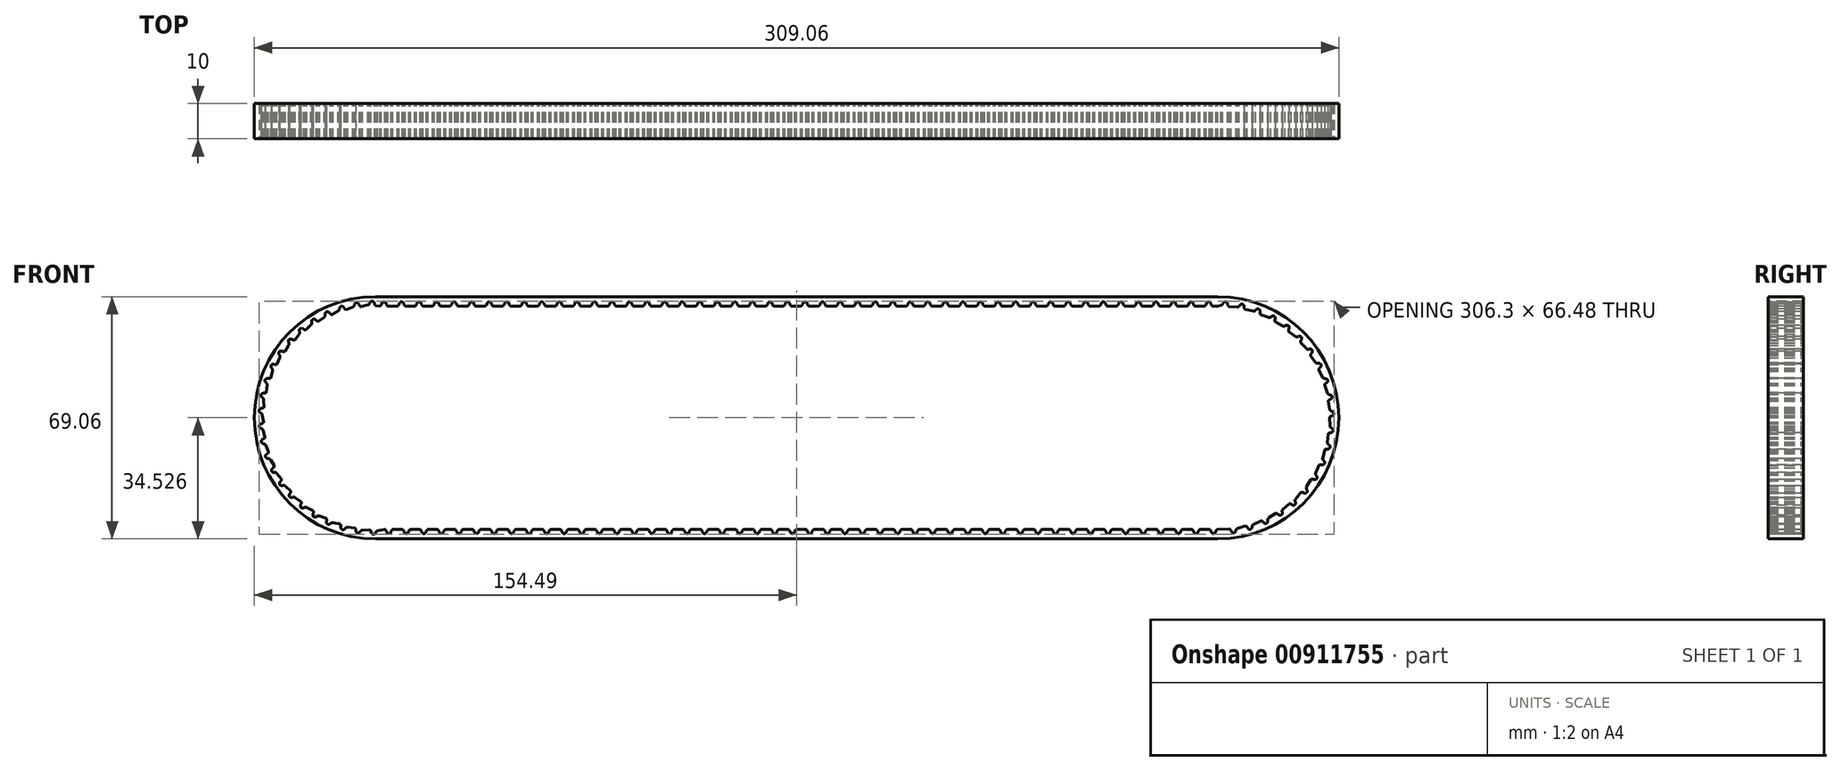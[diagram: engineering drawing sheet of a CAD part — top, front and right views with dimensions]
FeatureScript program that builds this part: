
annotation { "Feature Type Name" : "Feature", "Feature Type Description" : "" }
export const myFeature = defineFeature(function(context is Context, id is Id, definition is map)
    precondition{}
    {
        {
            var Q0;
            Q0=qCreatedBy(makeId("Front.planeOp"),FACE);
            var sketch = newSketch(context, id + "F0", { "sketchPlane" : qUnion([Q0])});
            skArc(sketch, "E0", {"start": v(-146.65, 34.53) * mm, "mid": v(-181.18, 0) * mm, "end": v(-146.65, -34.53) * mm});
            skArc(sketch, "E1", {"start": v(93.35, -34.53) * mm, "mid": v(127.88, 0) * mm, "end": v(93.35, 34.53) * mm});
            skLineSegment(sketch, "E2", {"start": v(93.35, 34.53) * mm, "end": v(-146.65, 34.53) * mm});
            skLineSegment(sketch, "E3", {"start": v(-146.65, 31.83) * mm, "end": v(-146.52, 31.83) * mm});
            skLineSegment(sketch, "E4", {"start": v(93.35, -34.53) * mm, "end": v(-146.65, -34.53) * mm});
            skLineSegment(sketch, "E5", {"start": v(93.35, -31.83) * mm, "end": v(-144, -31.83) * mm});
            skEllipticalArc(sketch, "E6.8.0.0", {});
            skArc(sketch, "E6.8.0.2", {"start": v(-103.52, 32.27) * mm, "mid": v(-103.35, 32) * mm, "end": v(-103.1, 31.83) * mm});
            skEllipticalArc(sketch, "E7.0.7.0", {});
            skArc(sketch, "E7.4.7.0", {"start": v(-105.44, 31.83) * mm, "mid": v(-105.14, 32) * mm, "end": v(-104.95, 32.27) * mm});
            skEllipticalArc(sketch, "E8.1.0.0", {});
            skArc(sketch, "E8.1.0.1", {"start": v(-98.52, 32.27) * mm, "mid": v(-98.35, 32) * mm, "end": v(-98.1, 31.83) * mm});
            skArc(sketch, "E8.1.0.2", {"start": v(-100.44, 31.83) * mm, "mid": v(-100.14, 32) * mm, "end": v(-99.95, 32.27) * mm});
            skEllipticalArc(sketch, "E8.1.0.3", {});
            skEllipticalArc(sketch, "E8.2.0.0", {});
            skArc(sketch, "E8.2.0.1", {"start": v(-93.52, 32.27) * mm, "mid": v(-93.35, 32) * mm, "end": v(-93.1, 31.83) * mm});
            skArc(sketch, "E8.2.0.2", {"start": v(-95.44, 31.83) * mm, "mid": v(-95.14, 32) * mm, "end": v(-94.95, 32.27) * mm});
            skEllipticalArc(sketch, "E8.2.0.3", {});
            skEllipticalArc(sketch, "E8.3.0.0", {});
            skArc(sketch, "E8.3.0.1", {"start": v(-88.52, 32.27) * mm, "mid": v(-88.35, 32) * mm, "end": v(-88.1, 31.83) * mm});
            skArc(sketch, "E8.3.0.2", {"start": v(-90.44, 31.83) * mm, "mid": v(-90.14, 32) * mm, "end": v(-89.95, 32.27) * mm});
            skEllipticalArc(sketch, "E8.3.0.3", {});
            skEllipticalArc(sketch, "E8.4.0.0", {});
            skArc(sketch, "E8.4.0.1", {"start": v(-83.52, 32.27) * mm, "mid": v(-83.35, 32) * mm, "end": v(-83.1, 31.83) * mm});
            skArc(sketch, "E8.4.0.2", {"start": v(-85.44, 31.83) * mm, "mid": v(-85.14, 32) * mm, "end": v(-84.95, 32.27) * mm});
            skEllipticalArc(sketch, "E8.4.0.3", {});
            skEllipticalArc(sketch, "E8.5.0.0", {});
            skArc(sketch, "E8.5.0.1", {"start": v(-78.52, 32.27) * mm, "mid": v(-78.35, 32) * mm, "end": v(-78.1, 31.83) * mm});
            skArc(sketch, "E8.5.0.2", {"start": v(-80.44, 31.83) * mm, "mid": v(-80.14, 32) * mm, "end": v(-79.95, 32.27) * mm});
            skEllipticalArc(sketch, "E8.5.0.3", {});
            skEllipticalArc(sketch, "E8.6.0.0", {});
            skArc(sketch, "E8.6.0.1", {"start": v(-73.52, 32.27) * mm, "mid": v(-73.35, 32) * mm, "end": v(-73.1, 31.83) * mm});
            skArc(sketch, "E8.6.0.2", {"start": v(-75.44, 31.83) * mm, "mid": v(-75.14, 32) * mm, "end": v(-74.95, 32.27) * mm});
            skEllipticalArc(sketch, "E8.6.0.3", {});
            skEllipticalArc(sketch, "E8.7.0.0", {});
            skArc(sketch, "E8.7.0.1", {"start": v(-68.52, 32.27) * mm, "mid": v(-68.35, 32) * mm, "end": v(-68.1, 31.83) * mm});
            skArc(sketch, "E8.7.0.2", {"start": v(-70.44, 31.83) * mm, "mid": v(-70.14, 32) * mm, "end": v(-69.95, 32.27) * mm});
            skEllipticalArc(sketch, "E8.7.0.3", {});
            skEllipticalArc(sketch, "E8.8.0.0", {});
            skArc(sketch, "E8.8.0.1", {"start": v(-63.52, 32.27) * mm, "mid": v(-63.35, 32) * mm, "end": v(-63.1, 31.83) * mm});
            skArc(sketch, "E8.8.0.2", {"start": v(-65.44, 31.83) * mm, "mid": v(-65.14, 32) * mm, "end": v(-64.95, 32.27) * mm});
            skEllipticalArc(sketch, "E8.8.0.3", {});
            skEllipticalArc(sketch, "E8.9.0.0", {});
            skArc(sketch, "E8.9.0.1", {"start": v(-58.52, 32.27) * mm, "mid": v(-58.35, 32) * mm, "end": v(-58.1, 31.83) * mm});
            skArc(sketch, "E8.9.0.2", {"start": v(-60.44, 31.83) * mm, "mid": v(-60.14, 32) * mm, "end": v(-59.95, 32.27) * mm});
            skEllipticalArc(sketch, "E8.9.0.3", {});
            skEllipticalArc(sketch, "E8.10.0.0", {});
            skArc(sketch, "E8.10.0.1", {"start": v(-53.52, 32.27) * mm, "mid": v(-53.35, 32) * mm, "end": v(-53.1, 31.83) * mm});
            skArc(sketch, "E8.10.0.2", {"start": v(-55.44, 31.83) * mm, "mid": v(-55.14, 32) * mm, "end": v(-54.95, 32.27) * mm});
            skEllipticalArc(sketch, "E8.10.0.3", {});
            skEllipticalArc(sketch, "E8.11.0.0", {});
            skArc(sketch, "E8.11.0.1", {"start": v(-48.52, 32.27) * mm, "mid": v(-48.35, 32) * mm, "end": v(-48.1, 31.83) * mm});
            skArc(sketch, "E8.11.0.2", {"start": v(-50.44, 31.83) * mm, "mid": v(-50.14, 32) * mm, "end": v(-49.95, 32.27) * mm});
            skEllipticalArc(sketch, "E8.11.0.3", {});
            skEllipticalArc(sketch, "E8.12.0.0", {});
            skArc(sketch, "E8.12.0.1", {"start": v(-43.52, 32.27) * mm, "mid": v(-43.35, 32) * mm, "end": v(-43.1, 31.83) * mm});
            skArc(sketch, "E8.12.0.2", {"start": v(-45.44, 31.83) * mm, "mid": v(-45.14, 32) * mm, "end": v(-44.95, 32.27) * mm});
            skEllipticalArc(sketch, "E8.12.0.3", {});
            skEllipticalArc(sketch, "E8.13.0.0", {});
            skArc(sketch, "E8.13.0.1", {"start": v(-38.52, 32.27) * mm, "mid": v(-38.35, 32) * mm, "end": v(-38.1, 31.83) * mm});
            skArc(sketch, "E8.13.0.2", {"start": v(-40.44, 31.83) * mm, "mid": v(-40.14, 32) * mm, "end": v(-39.95, 32.27) * mm});
            skEllipticalArc(sketch, "E8.13.0.3", {});
            skEllipticalArc(sketch, "E8.14.0.0", {});
            skArc(sketch, "E8.14.0.1", {"start": v(-33.52, 32.27) * mm, "mid": v(-33.35, 32) * mm, "end": v(-33.1, 31.83) * mm});
            skArc(sketch, "E8.14.0.2", {"start": v(-35.44, 31.83) * mm, "mid": v(-35.14, 32) * mm, "end": v(-34.95, 32.27) * mm});
            skEllipticalArc(sketch, "E8.14.0.3", {});
            skEllipticalArc(sketch, "E8.15.0.0", {});
            skArc(sketch, "E8.15.0.1", {"start": v(-28.52, 32.27) * mm, "mid": v(-28.35, 32) * mm, "end": v(-28.1, 31.83) * mm});
            skArc(sketch, "E8.15.0.2", {"start": v(-30.44, 31.83) * mm, "mid": v(-30.14, 32) * mm, "end": v(-29.95, 32.27) * mm});
            skEllipticalArc(sketch, "E8.15.0.3", {});
            skEllipticalArc(sketch, "E8.16.0.0", {});
            skArc(sketch, "E8.16.0.1", {"start": v(-23.52, 32.27) * mm, "mid": v(-23.35, 32) * mm, "end": v(-23.1, 31.83) * mm});
            skArc(sketch, "E8.16.0.2", {"start": v(-25.44, 31.83) * mm, "mid": v(-25.14, 32) * mm, "end": v(-24.95, 32.27) * mm});
            skEllipticalArc(sketch, "E8.16.0.3", {});
            skEllipticalArc(sketch, "E8.17.0.0", {});
            skArc(sketch, "E8.17.0.1", {"start": v(-18.52, 32.27) * mm, "mid": v(-18.35, 32) * mm, "end": v(-18.1, 31.83) * mm});
            skArc(sketch, "E8.17.0.2", {"start": v(-20.44, 31.83) * mm, "mid": v(-20.14, 32) * mm, "end": v(-19.95, 32.27) * mm});
            skEllipticalArc(sketch, "E8.17.0.3", {});
            skEllipticalArc(sketch, "E8.18.0.0", {});
            skArc(sketch, "E8.18.0.1", {"start": v(-13.52, 32.27) * mm, "mid": v(-13.35, 32) * mm, "end": v(-13.1, 31.83) * mm});
            skArc(sketch, "E8.18.0.2", {"start": v(-15.44, 31.83) * mm, "mid": v(-15.14, 32) * mm, "end": v(-14.95, 32.27) * mm});
            skEllipticalArc(sketch, "E8.18.0.3", {});
            skEllipticalArc(sketch, "E8.19.0.0", {});
            skArc(sketch, "E8.19.0.1", {"start": v(-8.52, 32.27) * mm, "mid": v(-8.35, 32) * mm, "end": v(-8.1, 31.83) * mm});
            skArc(sketch, "E8.19.0.2", {"start": v(-10.44, 31.83) * mm, "mid": v(-10.14, 32) * mm, "end": v(-9.95, 32.27) * mm});
            skEllipticalArc(sketch, "E8.19.0.3", {});
            skEllipticalArc(sketch, "E8.20.0.0", {});
            skArc(sketch, "E8.20.0.1", {"start": v(-3.52, 32.27) * mm, "mid": v(-3.35, 32) * mm, "end": v(-3.1, 31.83) * mm});
            skArc(sketch, "E8.20.0.2", {"start": v(-5.44, 31.83) * mm, "mid": v(-5.14, 32) * mm, "end": v(-4.95, 32.27) * mm});
            skEllipticalArc(sketch, "E8.20.0.3", {});
            skEllipticalArc(sketch, "E8.21.0.0", {});
            skArc(sketch, "E8.21.0.1", {"start": v(1.48, 32.27) * mm, "mid": v(1.65, 32) * mm, "end": v(1.9, 31.83) * mm});
            skArc(sketch, "E8.21.0.2", {"start": v(-0.44, 31.83) * mm, "mid": v(-0.14, 32) * mm, "end": v(0.05, 32.27) * mm});
            skEllipticalArc(sketch, "E8.21.0.3", {});
            skEllipticalArc(sketch, "E8.22.0.0", {});
            skArc(sketch, "E8.22.0.1", {"start": v(6.48, 32.27) * mm, "mid": v(6.65, 32) * mm, "end": v(6.9, 31.83) * mm});
            skArc(sketch, "E8.22.0.2", {"start": v(4.56, 31.83) * mm, "mid": v(4.86, 32) * mm, "end": v(5.05, 32.27) * mm});
            skEllipticalArc(sketch, "E8.22.0.3", {});
            skEllipticalArc(sketch, "E8.23.0.0", {});
            skArc(sketch, "E8.23.0.1", {"start": v(11.48, 32.27) * mm, "mid": v(11.65, 32) * mm, "end": v(11.9, 31.83) * mm});
            skArc(sketch, "E8.23.0.2", {"start": v(9.56, 31.83) * mm, "mid": v(9.86, 32) * mm, "end": v(10.05, 32.27) * mm});
            skEllipticalArc(sketch, "E8.23.0.3", {});
            skEllipticalArc(sketch, "E8.24.0.0", {});
            skArc(sketch, "E8.24.0.1", {"start": v(16.48, 32.27) * mm, "mid": v(16.65, 32) * mm, "end": v(16.9, 31.83) * mm});
            skArc(sketch, "E8.24.0.2", {"start": v(14.56, 31.83) * mm, "mid": v(14.86, 32) * mm, "end": v(15.05, 32.27) * mm});
            skEllipticalArc(sketch, "E8.24.0.3", {});
            skEllipticalArc(sketch, "E8.25.0.0", {});
            skArc(sketch, "E8.25.0.1", {"start": v(21.48, 32.27) * mm, "mid": v(21.65, 32) * mm, "end": v(21.9, 31.83) * mm});
            skArc(sketch, "E8.25.0.2", {"start": v(19.56, 31.83) * mm, "mid": v(19.86, 32) * mm, "end": v(20.05, 32.27) * mm});
            skEllipticalArc(sketch, "E8.25.0.3", {});
            skEllipticalArc(sketch, "E8.26.0.0", {});
            skArc(sketch, "E8.26.0.1", {"start": v(26.48, 32.27) * mm, "mid": v(26.65, 32) * mm, "end": v(26.9, 31.83) * mm});
            skArc(sketch, "E8.26.0.2", {"start": v(24.56, 31.83) * mm, "mid": v(24.86, 32) * mm, "end": v(25.05, 32.27) * mm});
            skEllipticalArc(sketch, "E8.26.0.3", {});
            skEllipticalArc(sketch, "E8.27.0.0", {});
            skArc(sketch, "E8.27.0.1", {"start": v(31.48, 32.27) * mm, "mid": v(31.65, 32) * mm, "end": v(31.9, 31.83) * mm});
            skArc(sketch, "E8.27.0.2", {"start": v(29.56, 31.83) * mm, "mid": v(29.86, 32) * mm, "end": v(30.05, 32.27) * mm});
            skEllipticalArc(sketch, "E8.27.0.3", {});
            skEllipticalArc(sketch, "E8.28.0.0", {});
            skArc(sketch, "E8.28.0.1", {"start": v(36.48, 32.27) * mm, "mid": v(36.65, 32) * mm, "end": v(36.9, 31.83) * mm});
            skArc(sketch, "E8.28.0.2", {"start": v(34.56, 31.83) * mm, "mid": v(34.86, 32) * mm, "end": v(35.05, 32.27) * mm});
            skEllipticalArc(sketch, "E8.28.0.3", {});
            skEllipticalArc(sketch, "E8.29.0.0", {});
            skArc(sketch, "E8.29.0.1", {"start": v(41.48, 32.27) * mm, "mid": v(41.65, 32) * mm, "end": v(41.9, 31.83) * mm});
            skArc(sketch, "E8.29.0.2", {"start": v(39.56, 31.83) * mm, "mid": v(39.86, 32) * mm, "end": v(40.05, 32.27) * mm});
            skEllipticalArc(sketch, "E8.29.0.3", {});
            skEllipticalArc(sketch, "E8.30.0.0", {});
            skArc(sketch, "E8.30.0.1", {"start": v(46.48, 32.27) * mm, "mid": v(46.65, 32) * mm, "end": v(46.9, 31.83) * mm});
            skArc(sketch, "E8.30.0.2", {"start": v(44.56, 31.83) * mm, "mid": v(44.86, 32) * mm, "end": v(45.05, 32.27) * mm});
            skEllipticalArc(sketch, "E8.30.0.3", {});
            skEllipticalArc(sketch, "E8.31.0.0", {});
            skArc(sketch, "E8.31.0.1", {"start": v(51.48, 32.27) * mm, "mid": v(51.65, 32) * mm, "end": v(51.9, 31.83) * mm});
            skArc(sketch, "E8.31.0.2", {"start": v(49.56, 31.83) * mm, "mid": v(49.86, 32) * mm, "end": v(50.05, 32.27) * mm});
            skEllipticalArc(sketch, "E8.31.0.3", {});
            skEllipticalArc(sketch, "E8.32.0.0", {});
            skArc(sketch, "E8.32.0.1", {"start": v(56.48, 32.27) * mm, "mid": v(56.65, 32) * mm, "end": v(56.9, 31.83) * mm});
            skArc(sketch, "E8.32.0.2", {"start": v(54.56, 31.83) * mm, "mid": v(54.86, 32) * mm, "end": v(55.05, 32.27) * mm});
            skEllipticalArc(sketch, "E8.32.0.3", {});
            skEllipticalArc(sketch, "E8.33.0.0", {});
            skArc(sketch, "E8.33.0.1", {"start": v(61.48, 32.27) * mm, "mid": v(61.65, 32) * mm, "end": v(61.9, 31.83) * mm});
            skArc(sketch, "E8.33.0.2", {"start": v(59.56, 31.83) * mm, "mid": v(59.86, 32) * mm, "end": v(60.05, 32.27) * mm});
            skEllipticalArc(sketch, "E8.33.0.3", {});
            skEllipticalArc(sketch, "E8.34.0.0", {});
            skArc(sketch, "E8.34.0.1", {"start": v(66.48, 32.27) * mm, "mid": v(66.65, 32) * mm, "end": v(66.9, 31.83) * mm});
            skArc(sketch, "E8.34.0.2", {"start": v(64.56, 31.83) * mm, "mid": v(64.86, 32) * mm, "end": v(65.05, 32.27) * mm});
            skEllipticalArc(sketch, "E8.34.0.3", {});
            skEllipticalArc(sketch, "E8.35.0.0", {});
            skArc(sketch, "E8.35.0.1", {"start": v(71.48, 32.27) * mm, "mid": v(71.65, 32) * mm, "end": v(71.9, 31.83) * mm});
            skArc(sketch, "E8.35.0.2", {"start": v(69.56, 31.83) * mm, "mid": v(69.86, 32) * mm, "end": v(70.05, 32.27) * mm});
            skEllipticalArc(sketch, "E8.35.0.3", {});
            skEllipticalArc(sketch, "E8.36.0.0", {});
            skArc(sketch, "E8.36.0.1", {"start": v(76.48, 32.27) * mm, "mid": v(76.65, 32) * mm, "end": v(76.9, 31.83) * mm});
            skArc(sketch, "E8.36.0.2", {"start": v(74.56, 31.83) * mm, "mid": v(74.86, 32) * mm, "end": v(75.05, 32.27) * mm});
            skEllipticalArc(sketch, "E8.36.0.3", {});
            skEllipticalArc(sketch, "E8.37.0.0", {});
            skArc(sketch, "E8.37.0.1", {"start": v(81.48, 32.27) * mm, "mid": v(81.65, 32) * mm, "end": v(81.9, 31.83) * mm});
            skArc(sketch, "E8.37.0.2", {"start": v(79.56, 31.83) * mm, "mid": v(79.86, 32) * mm, "end": v(80.05, 32.27) * mm});
            skEllipticalArc(sketch, "E8.37.0.3", {});
            skEllipticalArc(sketch, "E8.38.0.0", {});
            skArc(sketch, "E8.38.0.1", {"start": v(86.48, 32.27) * mm, "mid": v(86.65, 32) * mm, "end": v(86.9, 31.83) * mm});
            skArc(sketch, "E8.38.0.2", {"start": v(84.56, 31.83) * mm, "mid": v(84.86, 32) * mm, "end": v(85.05, 32.27) * mm});
            skEllipticalArc(sketch, "E8.38.0.3", {});
            skEllipticalArc(sketch, "E8.39.0.0", {});
            skArc(sketch, "E8.39.0.1", {"start": v(91.48, 32.27) * mm, "mid": v(91.65, 32) * mm, "end": v(91.9, 31.83) * mm});
            skArc(sketch, "E8.39.0.2", {"start": v(89.56, 31.83) * mm, "mid": v(89.86, 32) * mm, "end": v(90.05, 32.27) * mm});
            skEllipticalArc(sketch, "E8.39.0.3", {});
            skLineSegment(sketch, "E8.direction1", {"start": v(-105.44, 31.83) * mm, "end": v(-100.44, 31.83) * mm, "construction": true});
            skArc(sketch, "E9.1.0.0", {"start": v(-108.52, 32.27) * mm, "mid": v(-108.35, 32) * mm, "end": v(-108.1, 31.83) * mm});
            skEllipticalArc(sketch, "E9.1.0.1", {});
            skEllipticalArc(sketch, "E9.1.0.2", {});
            skArc(sketch, "E9.1.0.3", {"start": v(-110.44, 31.83) * mm, "mid": v(-110.14, 32) * mm, "end": v(-109.95, 32.27) * mm});
            skArc(sketch, "E9.2.0.0", {"start": v(-113.52, 32.27) * mm, "mid": v(-113.35, 32) * mm, "end": v(-113.1, 31.83) * mm});
            skEllipticalArc(sketch, "E9.2.0.1", {});
            skEllipticalArc(sketch, "E9.2.0.2", {});
            skArc(sketch, "E9.2.0.3", {"start": v(-115.44, 31.83) * mm, "mid": v(-115.14, 32) * mm, "end": v(-114.95, 32.27) * mm});
            skArc(sketch, "E9.3.0.0", {"start": v(-118.52, 32.27) * mm, "mid": v(-118.35, 32) * mm, "end": v(-118.1, 31.83) * mm});
            skEllipticalArc(sketch, "E9.3.0.1", {});
            skEllipticalArc(sketch, "E9.3.0.2", {});
            skArc(sketch, "E9.3.0.3", {"start": v(-120.44, 31.83) * mm, "mid": v(-120.14, 32) * mm, "end": v(-119.95, 32.27) * mm});
            skArc(sketch, "E9.4.0.0", {"start": v(-123.52, 32.27) * mm, "mid": v(-123.35, 32) * mm, "end": v(-123.1, 31.83) * mm});
            skEllipticalArc(sketch, "E9.4.0.1", {});
            skEllipticalArc(sketch, "E9.4.0.2", {});
            skArc(sketch, "E9.4.0.3", {"start": v(-125.44, 31.83) * mm, "mid": v(-125.14, 32) * mm, "end": v(-124.95, 32.27) * mm});
            skArc(sketch, "E9.5.0.0", {"start": v(-128.52, 32.27) * mm, "mid": v(-128.35, 32) * mm, "end": v(-128.1, 31.83) * mm});
            skEllipticalArc(sketch, "E9.5.0.1", {});
            skEllipticalArc(sketch, "E9.5.0.2", {});
            skArc(sketch, "E9.5.0.3", {"start": v(-130.44, 31.83) * mm, "mid": v(-130.14, 32) * mm, "end": v(-129.95, 32.27) * mm});
            skArc(sketch, "E9.6.0.0", {"start": v(-133.52, 32.27) * mm, "mid": v(-133.35, 32) * mm, "end": v(-133.1, 31.83) * mm});
            skEllipticalArc(sketch, "E9.6.0.1", {});
            skEllipticalArc(sketch, "E9.6.0.2", {});
            skArc(sketch, "E9.6.0.3", {"start": v(-135.44, 31.83) * mm, "mid": v(-135.14, 32) * mm, "end": v(-134.95, 32.27) * mm});
            skArc(sketch, "E9.7.0.0", {"start": v(-138.52, 32.27) * mm, "mid": v(-138.35, 32) * mm, "end": v(-138.1, 31.83) * mm});
            skEllipticalArc(sketch, "E9.7.0.1", {});
            skEllipticalArc(sketch, "E9.7.0.2", {});
            skArc(sketch, "E9.7.0.3", {"start": v(-140.44, 31.83) * mm, "mid": v(-140.14, 32) * mm, "end": v(-139.95, 32.27) * mm});
            skArc(sketch, "E9.8.0.0", {"start": v(-143.52, 32.27) * mm, "mid": v(-143.35, 32) * mm, "end": v(-143.1, 31.83) * mm});
            skEllipticalArc(sketch, "E9.8.0.1", {});
            skEllipticalArc(sketch, "E9.8.0.2", {});
            skArc(sketch, "E9.8.0.3", {"start": v(-145.44, 31.83) * mm, "mid": v(-145.14, 32) * mm, "end": v(-144.95, 32.27) * mm});
            skLineSegment(sketch, "E9.direction1", {"start": v(-103.1, 31.83) * mm, "end": v(-108.1, 31.83) * mm, "construction": true});
            skEllipticalArc(sketch, "E10.8.0.0", {});
            skArc(sketch, "E10.8.0.2", {"start": v(51.43, -32.27) * mm, "mid": v(51.26, -32) * mm, "end": v(51, -31.83) * mm});
            skEllipticalArc(sketch, "E11.0.7.0", {});
            skArc(sketch, "E11.4.7.0", {"start": v(53.35, -31.83) * mm, "mid": v(53.05, -32) * mm, "end": v(52.85, -32.27) * mm});
            skEllipticalArc(sketch, "E12.1.0.0", {});
            skArc(sketch, "E12.1.0.1", {"start": v(46.43, -32.27) * mm, "mid": v(46.26, -32) * mm, "end": v(46, -31.83) * mm});
            skArc(sketch, "E12.1.0.2", {"start": v(48.35, -31.83) * mm, "mid": v(48.05, -32) * mm, "end": v(47.85, -32.27) * mm});
            skEllipticalArc(sketch, "E12.1.0.3", {});
            skEllipticalArc(sketch, "E12.2.0.0", {});
            skArc(sketch, "E12.2.0.1", {"start": v(41.43, -32.27) * mm, "mid": v(41.26, -32) * mm, "end": v(41, -31.83) * mm});
            skArc(sketch, "E12.2.0.2", {"start": v(43.35, -31.83) * mm, "mid": v(43.05, -32) * mm, "end": v(42.85, -32.27) * mm});
            skEllipticalArc(sketch, "E12.2.0.3", {});
            skEllipticalArc(sketch, "E12.3.0.0", {});
            skArc(sketch, "E12.3.0.1", {"start": v(36.43, -32.27) * mm, "mid": v(36.26, -32) * mm, "end": v(36, -31.83) * mm});
            skArc(sketch, "E12.3.0.2", {"start": v(38.35, -31.83) * mm, "mid": v(38.05, -32) * mm, "end": v(37.85, -32.27) * mm});
            skEllipticalArc(sketch, "E12.3.0.3", {});
            skEllipticalArc(sketch, "E12.4.0.0", {});
            skArc(sketch, "E12.4.0.1", {"start": v(31.43, -32.27) * mm, "mid": v(31.26, -32) * mm, "end": v(31, -31.83) * mm});
            skArc(sketch, "E12.4.0.2", {"start": v(33.35, -31.83) * mm, "mid": v(33.05, -32) * mm, "end": v(32.85, -32.27) * mm});
            skEllipticalArc(sketch, "E12.4.0.3", {});
            skEllipticalArc(sketch, "E12.5.0.0", {});
            skArc(sketch, "E12.5.0.1", {"start": v(26.43, -32.27) * mm, "mid": v(26.26, -32) * mm, "end": v(26, -31.83) * mm});
            skArc(sketch, "E12.5.0.2", {"start": v(28.35, -31.83) * mm, "mid": v(28.05, -32) * mm, "end": v(27.85, -32.27) * mm});
            skEllipticalArc(sketch, "E12.5.0.3", {});
            skEllipticalArc(sketch, "E12.6.0.0", {});
            skArc(sketch, "E12.6.0.1", {"start": v(21.43, -32.27) * mm, "mid": v(21.26, -32) * mm, "end": v(21, -31.83) * mm});
            skArc(sketch, "E12.6.0.2", {"start": v(23.35, -31.83) * mm, "mid": v(23.05, -32) * mm, "end": v(22.85, -32.27) * mm});
            skEllipticalArc(sketch, "E12.6.0.3", {});
            skEllipticalArc(sketch, "E12.7.0.0", {});
            skArc(sketch, "E12.7.0.1", {"start": v(16.43, -32.27) * mm, "mid": v(16.26, -32) * mm, "end": v(16, -31.83) * mm});
            skArc(sketch, "E12.7.0.2", {"start": v(18.35, -31.83) * mm, "mid": v(18.05, -32) * mm, "end": v(17.85, -32.27) * mm});
            skEllipticalArc(sketch, "E12.7.0.3", {});
            skEllipticalArc(sketch, "E12.8.0.0", {});
            skArc(sketch, "E12.8.0.1", {"start": v(11.43, -32.27) * mm, "mid": v(11.26, -32) * mm, "end": v(11, -31.83) * mm});
            skArc(sketch, "E12.8.0.2", {"start": v(13.35, -31.83) * mm, "mid": v(13.05, -32) * mm, "end": v(12.85, -32.27) * mm});
            skEllipticalArc(sketch, "E12.8.0.3", {});
            skEllipticalArc(sketch, "E12.9.0.0", {});
            skArc(sketch, "E12.9.0.1", {"start": v(6.43, -32.27) * mm, "mid": v(6.26, -32) * mm, "end": v(6, -31.83) * mm});
            skArc(sketch, "E12.9.0.2", {"start": v(8.35, -31.83) * mm, "mid": v(8.05, -32) * mm, "end": v(7.85, -32.27) * mm});
            skEllipticalArc(sketch, "E12.9.0.3", {});
            skEllipticalArc(sketch, "E12.10.0.0", {});
            skArc(sketch, "E12.10.0.1", {"start": v(1.43, -32.27) * mm, "mid": v(1.26, -32) * mm, "end": v(1, -31.83) * mm});
            skArc(sketch, "E12.10.0.2", {"start": v(3.35, -31.83) * mm, "mid": v(3.05, -32) * mm, "end": v(2.85, -32.27) * mm});
            skEllipticalArc(sketch, "E12.10.0.3", {});
            skEllipticalArc(sketch, "E12.11.0.0", {});
            skArc(sketch, "E12.11.0.1", {"start": v(-3.57, -32.27) * mm, "mid": v(-3.74, -32) * mm, "end": v(-4, -31.83) * mm});
            skArc(sketch, "E12.11.0.2", {"start": v(-1.65, -31.83) * mm, "mid": v(-1.95, -32) * mm, "end": v(-2.15, -32.27) * mm});
            skEllipticalArc(sketch, "E12.11.0.3", {});
            skEllipticalArc(sketch, "E12.12.0.0", {});
            skArc(sketch, "E12.12.0.1", {"start": v(-8.57, -32.27) * mm, "mid": v(-8.74, -32) * mm, "end": v(-9, -31.83) * mm});
            skArc(sketch, "E12.12.0.2", {"start": v(-6.65, -31.83) * mm, "mid": v(-6.95, -32) * mm, "end": v(-7.15, -32.27) * mm});
            skEllipticalArc(sketch, "E12.12.0.3", {});
            skEllipticalArc(sketch, "E12.13.0.0", {});
            skArc(sketch, "E12.13.0.1", {"start": v(-13.57, -32.27) * mm, "mid": v(-13.74, -32) * mm, "end": v(-14, -31.83) * mm});
            skArc(sketch, "E12.13.0.2", {"start": v(-11.65, -31.83) * mm, "mid": v(-11.95, -32) * mm, "end": v(-12.15, -32.27) * mm});
            skEllipticalArc(sketch, "E12.13.0.3", {});
            skEllipticalArc(sketch, "E12.14.0.0", {});
            skArc(sketch, "E12.14.0.1", {"start": v(-18.57, -32.27) * mm, "mid": v(-18.74, -32) * mm, "end": v(-19, -31.83) * mm});
            skArc(sketch, "E12.14.0.2", {"start": v(-16.65, -31.83) * mm, "mid": v(-16.95, -32) * mm, "end": v(-17.15, -32.27) * mm});
            skEllipticalArc(sketch, "E12.14.0.3", {});
            skEllipticalArc(sketch, "E12.15.0.0", {});
            skArc(sketch, "E12.15.0.1", {"start": v(-23.57, -32.27) * mm, "mid": v(-23.74, -32) * mm, "end": v(-24, -31.83) * mm});
            skArc(sketch, "E12.15.0.2", {"start": v(-21.65, -31.83) * mm, "mid": v(-21.95, -32) * mm, "end": v(-22.15, -32.27) * mm});
            skEllipticalArc(sketch, "E12.15.0.3", {});
            skEllipticalArc(sketch, "E12.16.0.0", {});
            skArc(sketch, "E12.16.0.1", {"start": v(-28.57, -32.27) * mm, "mid": v(-28.74, -32) * mm, "end": v(-29, -31.83) * mm});
            skArc(sketch, "E12.16.0.2", {"start": v(-26.65, -31.83) * mm, "mid": v(-26.95, -32) * mm, "end": v(-27.15, -32.27) * mm});
            skEllipticalArc(sketch, "E12.16.0.3", {});
            skEllipticalArc(sketch, "E12.17.0.0", {});
            skArc(sketch, "E12.17.0.1", {"start": v(-33.57, -32.27) * mm, "mid": v(-33.74, -32) * mm, "end": v(-34, -31.83) * mm});
            skArc(sketch, "E12.17.0.2", {"start": v(-31.65, -31.83) * mm, "mid": v(-31.95, -32) * mm, "end": v(-32.15, -32.27) * mm});
            skEllipticalArc(sketch, "E12.17.0.3", {});
            skEllipticalArc(sketch, "E12.18.0.0", {});
            skArc(sketch, "E12.18.0.1", {"start": v(-38.57, -32.27) * mm, "mid": v(-38.74, -32) * mm, "end": v(-39, -31.83) * mm});
            skArc(sketch, "E12.18.0.2", {"start": v(-36.65, -31.83) * mm, "mid": v(-36.95, -32) * mm, "end": v(-37.15, -32.27) * mm});
            skEllipticalArc(sketch, "E12.18.0.3", {});
            skEllipticalArc(sketch, "E12.19.0.0", {});
            skArc(sketch, "E12.19.0.1", {"start": v(-43.57, -32.27) * mm, "mid": v(-43.74, -32) * mm, "end": v(-44, -31.83) * mm});
            skArc(sketch, "E12.19.0.2", {"start": v(-41.65, -31.83) * mm, "mid": v(-41.95, -32) * mm, "end": v(-42.15, -32.27) * mm});
            skEllipticalArc(sketch, "E12.19.0.3", {});
            skEllipticalArc(sketch, "E12.20.0.0", {});
            skArc(sketch, "E12.20.0.1", {"start": v(-48.57, -32.27) * mm, "mid": v(-48.74, -32) * mm, "end": v(-49, -31.83) * mm});
            skArc(sketch, "E12.20.0.2", {"start": v(-46.65, -31.83) * mm, "mid": v(-46.95, -32) * mm, "end": v(-47.15, -32.27) * mm});
            skEllipticalArc(sketch, "E12.20.0.3", {});
            skEllipticalArc(sketch, "E12.21.0.0", {});
            skArc(sketch, "E12.21.0.1", {"start": v(-53.57, -32.27) * mm, "mid": v(-53.74, -32) * mm, "end": v(-54, -31.83) * mm});
            skArc(sketch, "E12.21.0.2", {"start": v(-51.65, -31.83) * mm, "mid": v(-51.95, -32) * mm, "end": v(-52.15, -32.27) * mm});
            skEllipticalArc(sketch, "E12.21.0.3", {});
            skEllipticalArc(sketch, "E12.22.0.0", {});
            skArc(sketch, "E12.22.0.1", {"start": v(-58.57, -32.27) * mm, "mid": v(-58.74, -32) * mm, "end": v(-59, -31.83) * mm});
            skArc(sketch, "E12.22.0.2", {"start": v(-56.65, -31.83) * mm, "mid": v(-56.95, -32) * mm, "end": v(-57.15, -32.27) * mm});
            skEllipticalArc(sketch, "E12.22.0.3", {});
            skEllipticalArc(sketch, "E12.23.0.0", {});
            skArc(sketch, "E12.23.0.1", {"start": v(-63.57, -32.27) * mm, "mid": v(-63.74, -32) * mm, "end": v(-64, -31.83) * mm});
            skArc(sketch, "E12.23.0.2", {"start": v(-61.65, -31.83) * mm, "mid": v(-61.95, -32) * mm, "end": v(-62.15, -32.27) * mm});
            skEllipticalArc(sketch, "E12.23.0.3", {});
            skEllipticalArc(sketch, "E12.24.0.0", {});
            skArc(sketch, "E12.24.0.1", {"start": v(-68.57, -32.27) * mm, "mid": v(-68.74, -32) * mm, "end": v(-69, -31.83) * mm});
            skArc(sketch, "E12.24.0.2", {"start": v(-66.65, -31.83) * mm, "mid": v(-66.95, -32) * mm, "end": v(-67.15, -32.27) * mm});
            skEllipticalArc(sketch, "E12.24.0.3", {});
            skEllipticalArc(sketch, "E12.25.0.0", {});
            skArc(sketch, "E12.25.0.1", {"start": v(-73.57, -32.27) * mm, "mid": v(-73.74, -32) * mm, "end": v(-74, -31.83) * mm});
            skArc(sketch, "E12.25.0.2", {"start": v(-71.65, -31.83) * mm, "mid": v(-71.95, -32) * mm, "end": v(-72.15, -32.27) * mm});
            skEllipticalArc(sketch, "E12.25.0.3", {});
            skEllipticalArc(sketch, "E12.26.0.0", {});
            skArc(sketch, "E12.26.0.1", {"start": v(-78.57, -32.27) * mm, "mid": v(-78.74, -32) * mm, "end": v(-79, -31.83) * mm});
            skArc(sketch, "E12.26.0.2", {"start": v(-76.65, -31.83) * mm, "mid": v(-76.95, -32) * mm, "end": v(-77.15, -32.27) * mm});
            skEllipticalArc(sketch, "E12.26.0.3", {});
            skEllipticalArc(sketch, "E12.27.0.0", {});
            skArc(sketch, "E12.27.0.1", {"start": v(-83.57, -32.27) * mm, "mid": v(-83.74, -32) * mm, "end": v(-84, -31.83) * mm});
            skArc(sketch, "E12.27.0.2", {"start": v(-81.65, -31.83) * mm, "mid": v(-81.95, -32) * mm, "end": v(-82.15, -32.27) * mm});
            skEllipticalArc(sketch, "E12.27.0.3", {});
            skEllipticalArc(sketch, "E12.28.0.0", {});
            skArc(sketch, "E12.28.0.1", {"start": v(-88.57, -32.27) * mm, "mid": v(-88.74, -32) * mm, "end": v(-89, -31.83) * mm});
            skArc(sketch, "E12.28.0.2", {"start": v(-86.65, -31.83) * mm, "mid": v(-86.95, -32) * mm, "end": v(-87.15, -32.27) * mm});
            skEllipticalArc(sketch, "E12.28.0.3", {});
            skEllipticalArc(sketch, "E12.29.0.0", {});
            skArc(sketch, "E12.29.0.1", {"start": v(-93.57, -32.27) * mm, "mid": v(-93.74, -32) * mm, "end": v(-94, -31.83) * mm});
            skArc(sketch, "E12.29.0.2", {"start": v(-91.65, -31.83) * mm, "mid": v(-91.95, -32) * mm, "end": v(-92.15, -32.27) * mm});
            skEllipticalArc(sketch, "E12.29.0.3", {});
            skEllipticalArc(sketch, "E12.30.0.0", {});
            skArc(sketch, "E12.30.0.1", {"start": v(-98.57, -32.27) * mm, "mid": v(-98.74, -32) * mm, "end": v(-99, -31.83) * mm});
            skArc(sketch, "E12.30.0.2", {"start": v(-96.65, -31.83) * mm, "mid": v(-96.95, -32) * mm, "end": v(-97.15, -32.27) * mm});
            skEllipticalArc(sketch, "E12.30.0.3", {});
            skEllipticalArc(sketch, "E12.31.0.0", {});
            skArc(sketch, "E12.31.0.1", {"start": v(-103.57, -32.27) * mm, "mid": v(-103.74, -32) * mm, "end": v(-104, -31.83) * mm});
            skArc(sketch, "E12.31.0.2", {"start": v(-101.65, -31.83) * mm, "mid": v(-101.95, -32) * mm, "end": v(-102.15, -32.27) * mm});
            skEllipticalArc(sketch, "E12.31.0.3", {});
            skEllipticalArc(sketch, "E12.32.0.0", {});
            skArc(sketch, "E12.32.0.1", {"start": v(-108.57, -32.27) * mm, "mid": v(-108.74, -32) * mm, "end": v(-109, -31.83) * mm});
            skArc(sketch, "E12.32.0.2", {"start": v(-106.65, -31.83) * mm, "mid": v(-106.95, -32) * mm, "end": v(-107.15, -32.27) * mm});
            skEllipticalArc(sketch, "E12.32.0.3", {});
            skEllipticalArc(sketch, "E12.33.0.0", {});
            skArc(sketch, "E12.33.0.1", {"start": v(-113.57, -32.27) * mm, "mid": v(-113.74, -32) * mm, "end": v(-114, -31.83) * mm});
            skArc(sketch, "E12.33.0.2", {"start": v(-111.65, -31.83) * mm, "mid": v(-111.95, -32) * mm, "end": v(-112.15, -32.27) * mm});
            skEllipticalArc(sketch, "E12.33.0.3", {});
            skEllipticalArc(sketch, "E12.34.0.0", {});
            skArc(sketch, "E12.34.0.1", {"start": v(-118.57, -32.27) * mm, "mid": v(-118.74, -32) * mm, "end": v(-119, -31.83) * mm});
            skArc(sketch, "E12.34.0.2", {"start": v(-116.65, -31.83) * mm, "mid": v(-116.95, -32) * mm, "end": v(-117.15, -32.27) * mm});
            skEllipticalArc(sketch, "E12.34.0.3", {});
            skEllipticalArc(sketch, "E12.35.0.0", {});
            skArc(sketch, "E12.35.0.1", {"start": v(-123.57, -32.27) * mm, "mid": v(-123.74, -32) * mm, "end": v(-124, -31.83) * mm});
            skArc(sketch, "E12.35.0.2", {"start": v(-121.65, -31.83) * mm, "mid": v(-121.95, -32) * mm, "end": v(-122.15, -32.27) * mm});
            skEllipticalArc(sketch, "E12.35.0.3", {});
            skEllipticalArc(sketch, "E12.36.0.0", {});
            skArc(sketch, "E12.36.0.1", {"start": v(-128.57, -32.27) * mm, "mid": v(-128.74, -32) * mm, "end": v(-129, -31.83) * mm});
            skArc(sketch, "E12.36.0.2", {"start": v(-126.65, -31.83) * mm, "mid": v(-126.95, -32) * mm, "end": v(-127.15, -32.27) * mm});
            skEllipticalArc(sketch, "E12.36.0.3", {});
            skEllipticalArc(sketch, "E12.37.0.0", {});
            skArc(sketch, "E12.37.0.1", {"start": v(-133.57, -32.27) * mm, "mid": v(-133.74, -32) * mm, "end": v(-134, -31.83) * mm});
            skArc(sketch, "E12.37.0.2", {"start": v(-131.65, -31.83) * mm, "mid": v(-131.95, -32) * mm, "end": v(-132.15, -32.27) * mm});
            skEllipticalArc(sketch, "E12.37.0.3", {});
            skEllipticalArc(sketch, "E12.38.0.0", {});
            skArc(sketch, "E12.38.0.1", {"start": v(-138.57, -32.27) * mm, "mid": v(-138.74, -32) * mm, "end": v(-139, -31.83) * mm});
            skArc(sketch, "E12.38.0.2", {"start": v(-136.65, -31.83) * mm, "mid": v(-136.95, -32) * mm, "end": v(-137.15, -32.27) * mm});
            skEllipticalArc(sketch, "E12.38.0.3", {});
            skEllipticalArc(sketch, "E12.39.0.0", {});
            skArc(sketch, "E12.39.0.1", {"start": v(-143.57, -32.27) * mm, "mid": v(-143.74, -32) * mm, "end": v(-144, -31.83) * mm});
            skArc(sketch, "E12.39.0.2", {"start": v(-141.65, -31.83) * mm, "mid": v(-141.95, -32) * mm, "end": v(-142.15, -32.27) * mm});
            skEllipticalArc(sketch, "E12.39.0.3", {});
            skLineSegment(sketch, "E12.direction1", {"start": v(53.35, -31.83) * mm, "end": v(48.35, -31.83) * mm, "construction": true});
            skArc(sketch, "E13.1.0.0", {"start": v(56.43, -32.27) * mm, "mid": v(56.26, -32) * mm, "end": v(56, -31.83) * mm});
            skEllipticalArc(sketch, "E13.1.0.1", {});
            skEllipticalArc(sketch, "E13.1.0.2", {});
            skArc(sketch, "E13.1.0.3", {"start": v(58.35, -31.83) * mm, "mid": v(58.05, -32) * mm, "end": v(57.85, -32.27) * mm});
            skArc(sketch, "E13.2.0.0", {"start": v(61.43, -32.27) * mm, "mid": v(61.26, -32) * mm, "end": v(61, -31.83) * mm});
            skEllipticalArc(sketch, "E13.2.0.1", {});
            skEllipticalArc(sketch, "E13.2.0.2", {});
            skArc(sketch, "E13.2.0.3", {"start": v(63.35, -31.83) * mm, "mid": v(63.05, -32) * mm, "end": v(62.85, -32.27) * mm});
            skArc(sketch, "E13.3.0.0", {"start": v(66.43, -32.27) * mm, "mid": v(66.26, -32) * mm, "end": v(66, -31.83) * mm});
            skEllipticalArc(sketch, "E13.3.0.1", {});
            skEllipticalArc(sketch, "E13.3.0.2", {});
            skArc(sketch, "E13.3.0.3", {"start": v(68.35, -31.83) * mm, "mid": v(68.05, -32) * mm, "end": v(67.85, -32.27) * mm});
            skArc(sketch, "E13.4.0.0", {"start": v(71.43, -32.27) * mm, "mid": v(71.26, -32) * mm, "end": v(71, -31.83) * mm});
            skEllipticalArc(sketch, "E13.4.0.1", {});
            skEllipticalArc(sketch, "E13.4.0.2", {});
            skArc(sketch, "E13.4.0.3", {"start": v(73.35, -31.83) * mm, "mid": v(73.05, -32) * mm, "end": v(72.85, -32.27) * mm});
            skArc(sketch, "E13.5.0.0", {"start": v(76.43, -32.27) * mm, "mid": v(76.26, -32) * mm, "end": v(76, -31.83) * mm});
            skEllipticalArc(sketch, "E13.5.0.1", {});
            skEllipticalArc(sketch, "E13.5.0.2", {});
            skArc(sketch, "E13.5.0.3", {"start": v(78.35, -31.83) * mm, "mid": v(78.05, -32) * mm, "end": v(77.85, -32.27) * mm});
            skArc(sketch, "E13.6.0.0", {"start": v(81.43, -32.27) * mm, "mid": v(81.26, -32) * mm, "end": v(81, -31.83) * mm});
            skEllipticalArc(sketch, "E13.6.0.1", {});
            skEllipticalArc(sketch, "E13.6.0.2", {});
            skArc(sketch, "E13.6.0.3", {"start": v(83.35, -31.83) * mm, "mid": v(83.05, -32) * mm, "end": v(82.85, -32.27) * mm});
            skArc(sketch, "E13.7.0.0", {"start": v(86.43, -32.27) * mm, "mid": v(86.26, -32) * mm, "end": v(86, -31.83) * mm});
            skEllipticalArc(sketch, "E13.7.0.1", {});
            skEllipticalArc(sketch, "E13.7.0.2", {});
            skArc(sketch, "E13.7.0.3", {"start": v(88.35, -31.83) * mm, "mid": v(88.05, -32) * mm, "end": v(87.85, -32.27) * mm});
            skArc(sketch, "E13.8.0.0", {"start": v(91.43, -32.27) * mm, "mid": v(91.26, -32) * mm, "end": v(91, -31.83) * mm});
            skEllipticalArc(sketch, "E13.8.0.1", {});
            skEllipticalArc(sketch, "E13.8.0.2", {});
            skArc(sketch, "E13.8.0.3", {"start": v(93.35, -31.83) * mm, "mid": v(93.05, -32) * mm, "end": v(92.85, -32.27) * mm});
            skLineSegment(sketch, "E13.direction1", {"start": v(51, -31.83) * mm, "end": v(56, -31.83) * mm, "construction": true});
            skArc(sketch, "E14.1.0", {"start": v(-147.93, -32.4) * mm, "mid": v(-148.06, -32.1) * mm, "end": v(-148.3, -31.9) * mm});
            skEllipticalArc(sketch, "E14.1.1", {});
            skEllipticalArc(sketch, "E14.1.2", {});
            skArc(sketch, "E14.1.3", {"start": v(-145.97, -32.21) * mm, "mid": v(-146.28, -32.34) * mm, "end": v(-146.52, -32.59) * mm});
            skArc(sketch, "E14.2.0", {"start": v(-152.26, -31.93) * mm, "mid": v(-152.35, -31.63) * mm, "end": v(-152.56, -31.39) * mm});
            skEllipticalArc(sketch, "E14.2.1", {});
            skEllipticalArc(sketch, "E14.2.2", {});
            skArc(sketch, "E14.2.3", {"start": v(-150.3, -32.01) * mm, "mid": v(-150.63, -32.1) * mm, "end": v(-150.89, -32.31) * mm});
            skArc(sketch, "E14.3.0", {"start": v(-156.5, -30.89) * mm, "mid": v(-156.54, -30.58) * mm, "end": v(-156.71, -30.31) * mm});
            skEllipticalArc(sketch, "E14.3.1", {});
            skEllipticalArc(sketch, "E14.3.2", {});
            skArc(sketch, "E14.3.3", {"start": v(-154.55, -31.24) * mm, "mid": v(-154.9, -31.27) * mm, "end": v(-155.18, -31.45) * mm});
            skArc(sketch, "E14.4.0", {"start": v(-160.55, -29.3) * mm, "mid": v(-160.55, -28.98) * mm, "end": v(-160.69, -28.7) * mm});
            skEllipticalArc(sketch, "E14.4.1", {});
            skEllipticalArc(sketch, "E14.4.2", {});
            skArc(sketch, "E14.4.3", {"start": v(-158.67, -29.9) * mm, "mid": v(-159.01, -29.88) * mm, "end": v(-159.33, -30.02) * mm});
            skArc(sketch, "E14.5.0", {"start": v(-164.35, -27.16) * mm, "mid": v(-164.32, -26.85) * mm, "end": v(-164.4, -26.55) * mm});
            skEllipticalArc(sketch, "E14.5.1", {});
            skEllipticalArc(sketch, "E14.5.2", {});
            skArc(sketch, "E14.5.3", {"start": v(-162.57, -28.01) * mm, "mid": v(-162.9, -27.95) * mm, "end": v(-163.24, -28.05) * mm});
            skArc(sketch, "E14.6.0", {"start": v(-167.84, -24.54) * mm, "mid": v(-167.76, -24.24) * mm, "end": v(-167.81, -23.93) * mm});
            skEllipticalArc(sketch, "E14.6.1", {});
            skEllipticalArc(sketch, "E14.6.2", {});
            skArc(sketch, "E14.6.3", {"start": v(-166.19, -25.62) * mm, "mid": v(-166.51, -25.52) * mm, "end": v(-166.85, -25.57) * mm});
            skArc(sketch, "E14.7.0", {"start": v(-170.94, -21.48) * mm, "mid": v(-170.82, -21.19) * mm, "end": v(-170.83, -20.87) * mm});
            skEllipticalArc(sketch, "E14.7.1", {});
            skEllipticalArc(sketch, "E14.7.2", {});
            skArc(sketch, "E14.7.3", {"start": v(-169.45, -22.77) * mm, "mid": v(-169.76, -22.62) * mm, "end": v(-170.1, -22.63) * mm});
            skArc(sketch, "E14.8.0", {"start": v(-173.6, -18.03) * mm, "mid": v(-173.44, -17.75) * mm, "end": v(-173.4, -17.44) * mm});
            skEllipticalArc(sketch, "E14.8.1", {});
            skEllipticalArc(sketch, "E14.8.2", {});
            skArc(sketch, "E14.8.3", {"start": v(-172.3, -19.5) * mm, "mid": v(-172.58, -19.32) * mm, "end": v(-172.92, -19.28) * mm});
            skArc(sketch, "E14.9.0", {"start": v(-175.77, -14.25) * mm, "mid": v(-175.58, -14) * mm, "end": v(-175.5, -13.7) * mm});
            skEllipticalArc(sketch, "E14.9.1", {});
            skEllipticalArc(sketch, "E14.9.2", {});
            skArc(sketch, "E14.9.3", {"start": v(-174.68, -15.9) * mm, "mid": v(-174.94, -15.67) * mm, "end": v(-175.27, -15.58) * mm});
            skArc(sketch, "E14.10.0", {"start": v(-177.42, -10.21) * mm, "mid": v(-177.2, -10) * mm, "end": v(-177.08, -9.7) * mm});
            skEllipticalArc(sketch, "E14.10.1", {});
            skEllipticalArc(sketch, "E14.10.2", {});
            skArc(sketch, "E14.10.3", {"start": v(-176.56, -11.99) * mm, "mid": v(-176.78, -11.73) * mm, "end": v(-177.1, -11.6) * mm});
            skArc(sketch, "E14.11.0", {"start": v(-178.51, -6) * mm, "mid": v(-178.26, -5.8) * mm, "end": v(-178.1, -5.53) * mm});
            skEllipticalArc(sketch, "E14.11.1", {});
            skEllipticalArc(sketch, "E14.11.2", {});
            skArc(sketch, "E14.11.3", {"start": v(-177.9, -7.87) * mm, "mid": v(-178.09, -7.58) * mm, "end": v(-178.38, -7.41) * mm});
            skArc(sketch, "E14.12.0", {"start": v(-179.03, -1.67) * mm, "mid": v(-178.75, -1.51) * mm, "end": v(-178.57, -1.26) * mm});
            skEllipticalArc(sketch, "E14.12.1", {});
            skEllipticalArc(sketch, "E14.12.2", {});
            skArc(sketch, "E14.12.3", {"start": v(-178.67, -3.6) * mm, "mid": v(-178.82, -3.3) * mm, "end": v(-179.1, -3.1) * mm});
            skArc(sketch, "E14.13.0", {"start": v(-178.96, 2.7) * mm, "mid": v(-178.67, 2.8) * mm, "end": v(-178.45, 3.03) * mm});
            skEllipticalArc(sketch, "E14.13.1", {});
            skEllipticalArc(sketch, "E14.13.2", {});
            skArc(sketch, "E14.13.3", {"start": v(-178.86, 0.72) * mm, "mid": v(-178.97, 1.04) * mm, "end": v(-179.21, 1.29) * mm});
            skArc(sketch, "E14.14.0", {"start": v(-178.3, 7) * mm, "mid": v(-178, 7.07) * mm, "end": v(-177.75, 7.27) * mm});
            skEllipticalArc(sketch, "E14.14.1", {});
            skEllipticalArc(sketch, "E14.14.2", {});
            skArc(sketch, "E14.14.3", {"start": v(-178.48, 5.03) * mm, "mid": v(-178.54, 5.37) * mm, "end": v(-178.75, 5.64) * mm});
            skArc(sketch, "E14.15.0", {"start": v(-177.08, 11.18) * mm, "mid": v(-176.77, 11.22) * mm, "end": v(-176.5, 11.38) * mm});
            skEllipticalArc(sketch, "E14.15.1", {});
            skEllipticalArc(sketch, "E14.15.2", {});
            skArc(sketch, "E14.15.3", {"start": v(-177.51, 9.26) * mm, "mid": v(-177.53, 9.6) * mm, "end": v(-177.7, 9.9) * mm});
            skArc(sketch, "E14.16.0", {"start": v(-175.3, 15.16) * mm, "mid": v(-175, 15.15) * mm, "end": v(-174.7, 15.28) * mm});
            skEllipticalArc(sketch, "E14.16.1", {});
            skEllipticalArc(sketch, "E14.16.2", {});
            skArc(sketch, "E14.16.3", {"start": v(-176, 13.31) * mm, "mid": v(-175.96, 13.65) * mm, "end": v(-176.1, 13.97) * mm});
            skArc(sketch, "E14.17.0", {"start": v(-173.01, 18.87) * mm, "mid": v(-172.7, 18.82) * mm, "end": v(-172.4, 18.9) * mm});
            skEllipticalArc(sketch, "E14.17.1", {});
            skEllipticalArc(sketch, "E14.17.2", {});
            skArc(sketch, "E14.17.3", {"start": v(-173.94, 17.13) * mm, "mid": v(-173.87, 17.46) * mm, "end": v(-173.95, 17.8) * mm});
            skArc(sketch, "E14.18.0", {"start": v(-170.24, 22.24) * mm, "mid": v(-169.94, 22.14) * mm, "end": v(-169.63, 22.18) * mm});
            skEllipticalArc(sketch, "E14.18.1", {});
            skEllipticalArc(sketch, "E14.18.2", {});
            skArc(sketch, "E14.18.3", {"start": v(-171.4, 20.63) * mm, "mid": v(-171.28, 20.96) * mm, "end": v(-171.32, 21.3) * mm});
            skArc(sketch, "E14.19.0", {"start": v(-167.05, 25.2) * mm, "mid": v(-166.76, 25.07) * mm, "end": v(-166.45, 25.06) * mm});
            skEllipticalArc(sketch, "E14.19.1", {});
            skEllipticalArc(sketch, "E14.19.2", {});
            skArc(sketch, "E14.19.3", {"start": v(-168.4, 23.77) * mm, "mid": v(-168.25, 24.07) * mm, "end": v(-168.24, 24.41) * mm});
            skArc(sketch, "E14.20.0", {"start": v(-163.49, 27.7) * mm, "mid": v(-163.22, 27.54) * mm, "end": v(-162.9, 27.5) * mm});
            skEllipticalArc(sketch, "E14.20.1", {});
            skEllipticalArc(sketch, "E14.20.2", {});
            skArc(sketch, "E14.20.3", {"start": v(-165.02, 26.47) * mm, "mid": v(-164.82, 26.75) * mm, "end": v(-164.77, 27.09) * mm});
            skArc(sketch, "E14.21.0", {"start": v(-159.62, 29.72) * mm, "mid": v(-159.38, 29.51) * mm, "end": v(-159.07, 29.43) * mm});
            skEllipticalArc(sketch, "E14.21.1", {});
            skEllipticalArc(sketch, "E14.21.2", {});
            skArc(sketch, "E14.21.3", {"start": v(-161.3, 28.7) * mm, "mid": v(-161.07, 28.94) * mm, "end": v(-160.97, 29.27) * mm});
            skArc(sketch, "E14.22.0", {"start": v(-155.51, 31.19) * mm, "mid": v(-155.3, 30.95) * mm, "end": v(-155.01, 30.83) * mm});
            skEllipticalArc(sketch, "E14.22.1", {});
            skEllipticalArc(sketch, "E14.22.2", {});
            skArc(sketch, "E14.22.3", {"start": v(-157.32, 30.4) * mm, "mid": v(-157.06, 30.62) * mm, "end": v(-156.92, 30.93) * mm});
            skArc(sketch, "E14.23.0", {"start": v(-151.25, 32.1) * mm, "mid": v(-151.07, 31.83) * mm, "end": v(-150.8, 31.67) * mm});
            skEllipticalArc(sketch, "E14.23.1", {});
            skEllipticalArc(sketch, "E14.23.2", {});
            skArc(sketch, "E14.23.3", {"start": v(-153.15, 31.56) * mm, "mid": v(-152.86, 31.74) * mm, "end": v(-152.67, 32.03) * mm});
            skArc(sketch, "E14.24.0", {"start": v(-146.9, 32.42) * mm, "mid": v(-146.76, 32.14) * mm, "end": v(-146.52, 31.94) * mm});
            skEllipticalArc(sketch, "E14.24.1", {});
            skEllipticalArc(sketch, "E14.24.2", {});
            skArc(sketch, "E14.24.3", {"start": v(-148.86, 32.14) * mm, "mid": v(-148.54, 32.28) * mm, "end": v(-148.32, 32.54) * mm});
            skLineSegment(sketch, "E14.anchor1", {"start": v(-146.65, 0) * mm, "end": v(-144, -31.83) * mm, "construction": true});
            skLineSegment(sketch, "E14.anchor2", {"start": v(-146.65, 0) * mm, "end": v(-146.52, 31.94) * mm, "construction": true});
            skArc(sketch, "E15.1.0", {"start": v(96.22, 32.2) * mm, "mid": v(96.34, 31.91) * mm, "end": v(96.58, 31.7) * mm});
            skEllipticalArc(sketch, "E15.1.1", {});
            skEllipticalArc(sketch, "E15.1.2", {});
            skArc(sketch, "E15.1.3", {"start": v(94.25, 32.04) * mm, "mid": v(94.57, 32.16) * mm, "end": v(94.8, 32.4) * mm});
            skArc(sketch, "E15.2.0", {"start": v(100.9, 31.43) * mm, "mid": v(100.98, 31.13) * mm, "end": v(101.18, 30.89) * mm});
            skEllipticalArc(sketch, "E15.2.1", {});
            skEllipticalArc(sketch, "E15.2.2", {});
            skArc(sketch, "E15.2.3", {"start": v(98.93, 31.57) * mm, "mid": v(99.26, 31.64) * mm, "end": v(99.53, 31.85) * mm});
            skArc(sketch, "E15.3.0", {"start": v(105.41, 30) * mm, "mid": v(105.45, 29.68) * mm, "end": v(105.61, 29.4) * mm});
            skEllipticalArc(sketch, "E15.3.1", {});
            skEllipticalArc(sketch, "E15.3.2", {});
            skArc(sketch, "E15.3.3", {"start": v(103.49, 30.4) * mm, "mid": v(103.83, 30.43) * mm, "end": v(104.12, 30.6) * mm});
            skArc(sketch, "E15.4.0", {"start": v(109.67, 27.9) * mm, "mid": v(109.66, 27.6) * mm, "end": v(109.78, 27.3) * mm});
            skEllipticalArc(sketch, "E15.4.1", {});
            skEllipticalArc(sketch, "E15.4.2", {});
            skArc(sketch, "E15.4.3", {"start": v(107.82, 28.6) * mm, "mid": v(108.17, 28.57) * mm, "end": v(108.48, 28.7) * mm});
            skArc(sketch, "E15.5.0", {"start": v(113.58, 25.22) * mm, "mid": v(113.52, 24.9) * mm, "end": v(113.6, 24.6) * mm});
            skEllipticalArc(sketch, "E15.5.1", {});
            skEllipticalArc(sketch, "E15.5.2", {});
            skArc(sketch, "E15.5.3", {"start": v(111.85, 26.18) * mm, "mid": v(112.18, 26.1) * mm, "end": v(112.52, 26.17) * mm});
            skArc(sketch, "E15.6.0", {"start": v(117.05, 21.99) * mm, "mid": v(116.95, 21.7) * mm, "end": v(116.98, 21.38) * mm});
            skEllipticalArc(sketch, "E15.6.1", {});
            skEllipticalArc(sketch, "E15.6.2", {});
            skArc(sketch, "E15.6.3", {"start": v(115.48, 23.19) * mm, "mid": v(115.8, 23.06) * mm, "end": v(116.14, 23.09) * mm});
            skArc(sketch, "E15.7.0", {"start": v(120, 18.29) * mm, "mid": v(119.86, 18) * mm, "end": v(119.85, 17.7) * mm});
            skEllipticalArc(sketch, "E15.7.1", {});
            skEllipticalArc(sketch, "E15.7.2", {});
            skArc(sketch, "E15.7.3", {"start": v(118.63, 19.7) * mm, "mid": v(118.93, 19.53) * mm, "end": v(119.27, 19.5) * mm});
            skArc(sketch, "E15.8.0", {"start": v(122.4, 14.2) * mm, "mid": v(122.21, 13.94) * mm, "end": v(122.15, 13.63) * mm});
            skEllipticalArc(sketch, "E15.8.1", {});
            skEllipticalArc(sketch, "E15.8.2", {});
            skArc(sketch, "E15.8.3", {"start": v(121.24, 15.8) * mm, "mid": v(121.51, 15.58) * mm, "end": v(121.84, 15.5) * mm});
            skArc(sketch, "E15.9.0", {"start": v(124.16, 9.8) * mm, "mid": v(123.94, 9.57) * mm, "end": v(123.83, 9.27) * mm});
            skEllipticalArc(sketch, "E15.9.1", {});
            skEllipticalArc(sketch, "E15.9.2", {});
            skArc(sketch, "E15.9.3", {"start": v(123.25, 11.54) * mm, "mid": v(123.49, 11.3) * mm, "end": v(123.8, 11.17) * mm});
            skArc(sketch, "E15.10.0", {"start": v(125.26, 5.18) * mm, "mid": v(125, 4.99) * mm, "end": v(124.86, 4.71) * mm});
            skEllipticalArc(sketch, "E15.10.1", {});
            skEllipticalArc(sketch, "E15.10.2", {});
            skArc(sketch, "E15.10.3", {"start": v(124.62, 7.05) * mm, "mid": v(124.81, 6.77) * mm, "end": v(125.11, 6.6) * mm});
            skArc(sketch, "E15.11.0", {"start": v(125.67, 0.46) * mm, "mid": v(125.4, 0.3) * mm, "end": v(125.21, 0.05) * mm});
            skEllipticalArc(sketch, "E15.11.1", {});
            skEllipticalArc(sketch, "E15.11.2", {});
            skArc(sketch, "E15.11.3", {"start": v(125.31, 2.4) * mm, "mid": v(125.46, 2.1) * mm, "end": v(125.74, 1.88) * mm});
            skArc(sketch, "E15.12.0", {"start": v(125.4, -4.27) * mm, "mid": v(125.1, -4.38) * mm, "end": v(124.88, -4.6) * mm});
            skEllipticalArc(sketch, "E15.12.1", {});
            skEllipticalArc(sketch, "E15.12.2", {});
            skArc(sketch, "E15.12.3", {"start": v(125.32, -2.3) * mm, "mid": v(125.43, -2.63) * mm, "end": v(125.66, -2.87) * mm});
            skArc(sketch, "E15.13.0", {"start": v(124.42, -8.91) * mm, "mid": v(124.12, -8.98) * mm, "end": v(123.86, -9.17) * mm});
            skEllipticalArc(sketch, "E15.13.1", {});
            skEllipticalArc(sketch, "E15.13.2", {});
            skArc(sketch, "E15.13.3", {"start": v(124.64, -6.95) * mm, "mid": v(124.7, -7.29) * mm, "end": v(124.9, -7.57) * mm});
            skArc(sketch, "E15.14.0", {"start": v(122.79, -13.36) * mm, "mid": v(122.47, -13.38) * mm, "end": v(122.2, -13.53) * mm});
            skEllipticalArc(sketch, "E15.14.1", {});
            skEllipticalArc(sketch, "E15.14.2", {});
            skArc(sketch, "E15.14.3", {"start": v(123.29, -11.45) * mm, "mid": v(123.3, -11.8) * mm, "end": v(123.45, -12.1) * mm});
            skArc(sketch, "E15.15.0", {"start": v(120.52, -17.52) * mm, "mid": v(120.2, -17.5) * mm, "end": v(119.9, -17.6) * mm});
            skEllipticalArc(sketch, "E15.15.1", {});
            skEllipticalArc(sketch, "E15.15.2", {});
            skArc(sketch, "E15.15.3", {"start": v(121.3, -15.7) * mm, "mid": v(121.25, -16.05) * mm, "end": v(121.36, -16.37) * mm});
            skArc(sketch, "E15.16.0", {"start": v(117.66, -21.3) * mm, "mid": v(117.35, -21.24) * mm, "end": v(117.05, -21.3) * mm});
            skEllipticalArc(sketch, "E15.16.1", {});
            skEllipticalArc(sketch, "E15.16.2", {});
            skArc(sketch, "E15.16.3", {"start": v(118.7, -19.63) * mm, "mid": v(118.6, -19.96) * mm, "end": v(118.66, -20.3) * mm});
            skArc(sketch, "E15.17.0", {"start": v(114.28, -24.63) * mm, "mid": v(114, -24.52) * mm, "end": v(113.68, -24.54) * mm});
            skEllipticalArc(sketch, "E15.17.1", {});
            skEllipticalArc(sketch, "E15.17.2", {});
            skArc(sketch, "E15.17.3", {"start": v(115.55, -23.12) * mm, "mid": v(115.4, -23.43) * mm, "end": v(115.42, -23.78) * mm});
            skArc(sketch, "E15.18.0", {"start": v(110.46, -27.43) * mm, "mid": v(110.18, -27.27) * mm, "end": v(109.87, -27.25) * mm});
            skEllipticalArc(sketch, "E15.18.1", {});
            skEllipticalArc(sketch, "E15.18.2", {});
            skArc(sketch, "E15.18.3", {"start": v(111.93, -26.12) * mm, "mid": v(111.75, -26.4) * mm, "end": v(111.7, -26.75) * mm});
            skArc(sketch, "E15.19.0", {"start": v(106.26, -29.64) * mm, "mid": v(106.01, -29.44) * mm, "end": v(105.7, -29.37) * mm});
            skEllipticalArc(sketch, "E15.19.1", {});
            skEllipticalArc(sketch, "E15.19.2", {});
            skArc(sketch, "E15.19.3", {"start": v(107.91, -28.56) * mm, "mid": v(107.69, -28.81) * mm, "end": v(107.6, -29.14) * mm});
            skArc(sketch, "E15.20.0", {"start": v(101.79, -31.2) * mm, "mid": v(101.57, -30.98) * mm, "end": v(101.28, -30.86) * mm});
            skEllipticalArc(sketch, "E15.20.1", {});
            skEllipticalArc(sketch, "E15.20.2", {});
            skArc(sketch, "E15.20.3", {"start": v(103.58, -30.38) * mm, "mid": v(103.32, -30.6) * mm, "end": v(103.18, -30.92) * mm});
            skArc(sketch, "E15.21.0", {"start": v(97.13, -32.1) * mm, "mid": v(96.95, -31.85) * mm, "end": v(96.68, -31.69) * mm});
            skEllipticalArc(sketch, "E15.21.1", {});
            skEllipticalArc(sketch, "E15.21.2", {});
            skArc(sketch, "E15.21.3", {"start": v(99.03, -31.55) * mm, "mid": v(98.74, -31.73) * mm, "end": v(98.56, -32.02) * mm});
            skLineSegment(sketch, "E15.anchor1", {"start": v(93.35, 0) * mm, "end": v(89.56, 31.83) * mm, "construction": true});
            skLineSegment(sketch, "E15.anchor2", {"start": v(93.35, 0) * mm, "end": v(94.35, -32.04) * mm, "construction": true});
            skLineSegment(sketch, "E16", {"start": v(93.35, 31.83) * mm, "end": v(94.25, 32.04) * mm});
            skLineSegment(sketch, "E17", {"start": v(96.58, 31.7) * mm, "end": v(98.93, 31.57) * mm});
            skLineSegment(sketch, "E18", {"start": v(101.18, 30.89) * mm, "end": v(103.49, 30.4) * mm});
            skLineSegment(sketch, "E19", {"start": v(105.61, 29.4) * mm, "end": v(107.82, 28.6) * mm});
            skLineSegment(sketch, "E20", {"start": v(109.78, 27.3) * mm, "end": v(111.85, 26.18) * mm});
            skLineSegment(sketch, "E21", {"start": v(113.6, 24.6) * mm, "end": v(115.48, 23.19) * mm});
            skLineSegment(sketch, "E22", {"start": v(116.98, 21.38) * mm, "end": v(118.63, 19.7) * mm});
            skLineSegment(sketch, "E23", {"start": v(119.85, 17.7) * mm, "end": v(121.24, 15.8) * mm});
            skLineSegment(sketch, "E24", {"start": v(122.15, 13.63) * mm, "end": v(123.25, 11.54) * mm});
            skLineSegment(sketch, "E25", {"start": v(123.83, 9.27) * mm, "end": v(124.62, 7.05) * mm});
            skLineSegment(sketch, "E26", {"start": v(124.86, 4.71) * mm, "end": v(125.31, 2.4) * mm});
            skLineSegment(sketch, "E27", {"start": v(125.21, 0.05) * mm, "end": v(125.32, -2.3) * mm});
            skLineSegment(sketch, "E28", {"start": v(124.88, -4.6) * mm, "end": v(124.64, -6.95) * mm});
            skLineSegment(sketch, "E29", {"start": v(123.86, -9.17) * mm, "end": v(123.29, -11.45) * mm});
            skLineSegment(sketch, "E30", {"start": v(122.2, -13.53) * mm, "end": v(121.3, -15.7) * mm});
            skLineSegment(sketch, "E31", {"start": v(119.9, -17.6) * mm, "end": v(118.7, -19.63) * mm});
            skLineSegment(sketch, "E32", {"start": v(117.05, -21.3) * mm, "end": v(115.55, -23.12) * mm});
            skLineSegment(sketch, "E33", {"start": v(113.68, -24.54) * mm, "end": v(111.93, -26.12) * mm});
            skLineSegment(sketch, "E34", {"start": v(109.87, -27.25) * mm, "end": v(107.91, -28.56) * mm});
            skLineSegment(sketch, "E35", {"start": v(105.7, -29.37) * mm, "end": v(103.58, -30.38) * mm});
            skLineSegment(sketch, "E36", {"start": v(101.28, -30.86) * mm, "end": v(99.03, -31.55) * mm});
            skLineSegment(sketch, "E37", {"start": v(96.68, -31.69) * mm, "end": v(93.35, -31.83) * mm});
            skLineSegment(sketch, "E38", {"start": v(-144, -31.83) * mm, "end": v(-145.97, -32.21) * mm});
            skPoint(sketch, "E39.orphan", {"position": v(-146.65, -31.83) * mm});
            skLineSegment(sketch, "E40", {"start": v(-148.3, -31.9) * mm, "end": v(-150.3, -32.01) * mm});
            skLineSegment(sketch, "E41", {"start": v(-152.56, -31.39) * mm, "end": v(-154.55, -31.24) * mm});
            skLineSegment(sketch, "E42", {"start": v(-156.71, -30.31) * mm, "end": v(-158.67, -29.9) * mm});
            skLineSegment(sketch, "E43", {"start": v(-160.69, -28.7) * mm, "end": v(-162.57, -28.01) * mm});
            skLineSegment(sketch, "E44", {"start": v(-164.4, -26.55) * mm, "end": v(-166.19, -25.62) * mm});
            skLineSegment(sketch, "E45", {"start": v(-167.81, -23.93) * mm, "end": v(-169.45, -22.77) * mm});
            skLineSegment(sketch, "E46", {"start": v(-170.83, -20.87) * mm, "end": v(-172.3, -19.5) * mm});
            skLineSegment(sketch, "E47", {"start": v(-173.4, -17.44) * mm, "end": v(-174.68, -15.9) * mm});
            skLineSegment(sketch, "E48", {"start": v(-175.5, -13.7) * mm, "end": v(-176.56, -11.99) * mm});
            skLineSegment(sketch, "E49", {"start": v(-177.08, -9.7) * mm, "end": v(-177.9, -7.87) * mm});
            skLineSegment(sketch, "E50", {"start": v(-178.1, -5.53) * mm, "end": v(-178.67, -3.6) * mm});
            skLineSegment(sketch, "E51", {"start": v(-178.57, -1.26) * mm, "end": v(-178.86, 0.72) * mm});
            skLineSegment(sketch, "E52", {"start": v(-178.45, 3.03) * mm, "end": v(-178.48, 5.03) * mm});
            skLineSegment(sketch, "E53", {"start": v(-177.75, 7.27) * mm, "end": v(-177.51, 9.26) * mm});
            skLineSegment(sketch, "E54", {"start": v(-176.5, 11.38) * mm, "end": v(-176, 13.31) * mm});
            skLineSegment(sketch, "E55", {"start": v(-174.7, 15.28) * mm, "end": v(-173.94, 17.13) * mm});
            skLineSegment(sketch, "E56", {"start": v(-172.4, 18.9) * mm, "end": v(-171.4, 20.63) * mm});
            skLineSegment(sketch, "E57", {"start": v(-169.63, 22.18) * mm, "end": v(-168.4, 23.77) * mm});
            skLineSegment(sketch, "E58", {"start": v(-166.45, 25.06) * mm, "end": v(-165.02, 26.47) * mm});
            skLineSegment(sketch, "E59", {"start": v(-162.9, 27.5) * mm, "end": v(-161.3, 28.7) * mm});
            skLineSegment(sketch, "E60", {"start": v(-159.07, 29.43) * mm, "end": v(-157.32, 30.4) * mm});
            skLineSegment(sketch, "E61", {"start": v(-155.01, 30.83) * mm, "end": v(-153.15, 31.56) * mm});
            skLineSegment(sketch, "E62", {"start": v(-150.8, 31.67) * mm, "end": v(-148.86, 32.14) * mm});
            skLineSegment(sketch, "E63", {"start": v(-146.52, 31.94) * mm, "end": v(-145.44, 31.83) * mm});
            skLineSegment(sketch, "E64.trimOffspring", {"start": v(-145.44, 31.83) * mm, "end": v(93.35, 31.83) * mm});
            const initialGuessF0  = {"E6.8.0.0": [-0.10424721509218197, 0.03203, 0, 1, 0.001, 0.00075, 4.958959793330999, 0], "E7.0.7.0": [-0.10424721509218215, 0.03203, 0, 1, 0.001, 0.0007199110732306023, 0, 1.3242255138486574], "E8.1.0.0": [-0.09924721509218215, 0.03203, 0, 1, 0.001, 0.0007199110732306023, 0, 1.3242255138486574], "E8.1.0.3": [-0.09924721509218197, 0.03203, 0, 1, 0.001, 0.00075, 4.958959793330999, 0], "E8.2.0.0": [-0.09424721509218215, 0.03203, 0, 1, 0.001, 0.0007199110732306023, 0, 1.3242255138486574], "E8.2.0.3": [-0.09424721509218197, 0.03203, 0, 1, 0.001, 0.00075, 4.958959793330999, 0], "E8.3.0.0": [-0.08924721509218214, 0.03203, 0, 1, 0.001, 0.0007199110732306023, 0, 1.3242255138486574], "E8.3.0.3": [-0.08924721509218196, 0.03203, 0, 1, 0.001, 0.00075, 4.958959793330999, 0], "E8.4.0.0": [-0.08424721509218214, 0.03203, 0, 1, 0.001, 0.0007199110732306023, 0, 1.3242255138486574], "E8.4.0.3": [-0.08424721509218196, 0.03203, 0, 1, 0.001, 0.00075, 4.958959793330992, 0], "E8.5.0.0": [-0.07924721509218213, 0.03203, 0, 1, 0.001, 0.0007199110732306023, 0, 1.3242255138486574], "E8.5.0.3": [-0.07924721509218195, 0.03203, 0, 1, 0.001, 0.00075, 4.958959793330992, 0], "E8.6.0.0": [-0.07424721509218213, 0.03203, 0, 1, 0.001, 0.0007199110732306023, 0, 1.3242255138486574], "E8.6.0.3": [-0.07424721509218196, 0.03203, 0, 1, 0.001, 0.00075, 4.9589597933309895, 0], "E8.7.0.0": [-0.06924721509218212, 0.03203, 0, 1, 0.001, 0.0007199110732306023, 0, 1.3242255138486574], "E8.7.0.3": [-0.06924721509218196, 0.03203, 0, 1, 0.001, 0.00075, 4.9589597933309895, 0], "E8.8.0.0": [-0.06424721509218212, 0.03203, 0, 1, 0.001, 0.0007199110732306023, 0, 1.3242255138486574], "E8.8.0.3": [-0.06424721509218195, 0.03203, 0, 1, 0.001, 0.00075, 4.9589597933309895, 0], "E8.9.0.0": [-0.059247215092182115, 0.03203, 0, 1, 0.001, 0.0007199110732306023, 0, 1.3242255138486574], "E8.9.0.3": [-0.05924721509218194, 0.03203, 0, 1, 0.001, 0.00075, 4.95895979333099, 6.283185307179582], "E8.10.0.0": [-0.05424721509218211, 0.03203, 0, 1, 0.001, 0.0007199110732306023, 0, 1.3242255138486574], "E8.10.0.3": [-0.05424721509218194, 0.03203, 0, 1, 0.001, 0.00075, 4.95895979333099, 6.283185307179582], "E8.11.0.0": [-0.049247215092182106, 0.03203, 0, 1, 0.001, 0.0007199110732306023, 0, 1.3242255138486574], "E8.11.0.3": [-0.04924721509218193, 0.03203, 0, 1, 0.001, 0.00075, 4.95895979333099, 6.283185307179582], "E8.12.0.0": [-0.0442472150921821, 0.03203, 0, 1, 0.001, 0.0007199110732306023, 0, 1.3242255138486574], "E8.12.0.3": [-0.044247215092181935, 0.03203, 0, 1, 0.001, 0.00075, 4.958959793330982, 6.283185307179582], "E8.13.0.0": [-0.0392472150921821, 0.03203, 0, 1, 0.001, 0.0007199110732306023, 0, 1.3242255138486574], "E8.13.0.3": [-0.03924721509218193, 0.03203, 0, 1, 0.001, 0.00075, 4.958959793330982, 6.283185307179582], "E8.14.0.0": [-0.03424721509218209, 0.03203, 0, 1, 0.001, 0.0007199110732306023, 0, 1.3242255138486574], "E8.14.0.3": [-0.034247215092181926, 0.03203, 0, 1, 0.001, 0.00075, 4.958959793330982, 6.283185307179582], "E8.15.0.0": [-0.02924721509218209, 0.03203, 0, 1, 0.001, 0.0007199110732306023, 0, 1.3242255138486574], "E8.15.0.3": [-0.029247215092181922, 0.03203, 0, 1, 0.001, 0.00075, 4.958959793330983, 0], "E8.16.0.0": [-0.024247215092182084, 0.03203, 0, 1, 0.001, 0.0007199110732306023, 0, 1.3242255138486574], "E8.16.0.3": [-0.024247215092181917, 0.03203, 0, 1, 0.001, 0.00075, 4.958959793330983, 0], "E8.17.0.0": [-0.01924721509218208, 0.03203, 0, 1, 0.001, 0.0007199110732306023, 0, 1.3242255138486574], "E8.17.0.3": [-0.019247215092181913, 0.03203, 0, 1, 0.001, 0.00075, 4.958959793330983, 0], "E8.18.0.0": [-0.014247215092182075, 0.03203, 0, 1, 0.001, 0.0007199110732306023, 0, 1.3242255138486574], "E8.18.0.3": [-0.014247215092181909, 0.03203, 0, 1, 0.001, 0.00075, 4.958959793330983, 0], "E8.19.0.0": [-0.00924721509218207, 0.03203, 0, 1, 0.001, 0.0007199110732306023, 0, 1.3242255138486574], "E8.19.0.3": [-0.009247215092181904, 0.03203, 0, 1, 0.001, 0.00075, 4.958959793330976, 0], "E8.20.0.0": [-0.004247215092182066, 0.03203, 0, 1, 0.001, 0.0007199110732306023, 0, 1.3242255138486574], "E8.20.0.3": [-0.0042472150921819, 0.03203, 0, 1, 0.001, 0.00075, 4.958959793330976, 0], "E8.21.0.0": [0.0007527849078179383, 0.03203, 0, 1, 0.001, 0.0007199110732306023, 0, 1.3242255138486574], "E8.21.0.3": [0.0007527849078181048, 0.03203, 0, 1, 0.001, 0.00075, 4.958959793330976, 0], "E8.22.0.0": [0.005752784907817943, 0.03203, 0, 1, 0.001, 0.0007199110732306023, 0, 1.3242255138486574], "E8.22.0.3": [0.005752784907818109, 0.03203, 0, 1, 0.001, 0.00075, 4.958959793330976, 0], "E8.23.0.0": [0.010752784907817947, 0.03203, 0, 1, 0.001, 0.0007199110732306023, 0, 1.3242255138486574], "E8.23.0.3": [0.010752784907818114, 0.03203, 0, 1, 0.001, 0.00075, 4.958959793330976, 0], "E8.24.0.0": [0.01575278490781795, 0.03203, 0, 1, 0.001, 0.0007199110732306023, 0, 1.3242255138486574], "E8.24.0.3": [0.015752784907818104, 0.03203, 0, 1, 0.001, 0.00075, 4.9589597933309735, 0], "E8.25.0.0": [0.020752784907817956, 0.03203, 0, 1, 0.001, 0.0007199110732306023, 0, 1.3242255138486574], "E8.25.0.3": [0.02075278490781811, 0.03203, 0, 1, 0.001, 0.00075, 4.9589597933309735, 0], "E8.26.0.0": [0.02575278490781796, 0.03203, 0, 1, 0.001, 0.0007199110732306023, 0, 1.3242255138486574], "E8.26.0.3": [0.025752784907818113, 0.03203, 0, 1, 0.001, 0.00075, 4.9589597933309735, 0], "E8.27.0.0": [0.030752784907817965, 0.03203, 0, 1, 0.001, 0.0007199110732306023, 0, 1.3242255138486574], "E8.27.0.3": [0.030752784907818118, 0.03203, 0, 1, 0.001, 0.00075, 4.958959793330966, 0], "E8.28.0.0": [0.03575278490781797, 0.03203, 0, 1, 0.001, 0.0007199110732306023, 0, 1.3242255138486574], "E8.28.0.3": [0.03575278490781812, 0.03203, 0, 1, 0.001, 0.00075, 4.958959793330966, 6.283185307179582], "E8.29.0.0": [0.040752784907817974, 0.03203, 0, 1, 0.001, 0.0007199110732306023, 0, 1.3242255138486574], "E8.29.0.3": [0.040752784907818126, 0.03203, 0, 1, 0.001, 0.00075, 4.958959793330966, 6.283185307179582], "E8.30.0.0": [0.04575278490781798, 0.03203, 0, 1, 0.001, 0.0007199110732306023, 0, 1.3242255138486574], "E8.30.0.3": [0.04575278490781813, 0.03203, 0, 1, 0.001, 0.00075, 4.958959793330966, 6.283185307179582], "E8.31.0.0": [0.05075278490781798, 0.03203, 0, 1, 0.001, 0.0007199110732306023, 0, 1.3242255138486574], "E8.31.0.3": [0.050752784907818135, 0.03203, 0, 1, 0.001, 0.00075, 4.958959793330966, 6.283185307179582], "E8.32.0.0": [0.05575278490781799, 0.03203, 0, 1, 0.001, 0.0007199110732306023, 0, 1.3242255138486574], "E8.32.0.3": [0.05575278490781814, 0.03203, 0, 1, 0.001, 0.00075, 4.958959793330966, 6.283185307179582], "E8.33.0.0": [0.06075278490781799, 0.03203, 0, 1, 0.001, 0.0007199110732306023, 0, 1.3242255138486574], "E8.33.0.3": [0.060752784907818144, 0.03203, 0, 1, 0.001, 0.00075, 4.958959793330966, 6.283185307179582], "E8.34.0.0": [0.065752784907818, 0.03203, 0, 1, 0.001, 0.0007199110732306023, 0, 1.3242255138486574], "E8.34.0.3": [0.06575278490781815, 0.03203, 0, 1, 0.001, 0.00075, 4.958959793330959, 0], "E8.35.0.0": [0.070752784907818, 0.03203, 0, 1, 0.001, 0.0007199110732306023, 0, 1.3242255138486574], "E8.35.0.3": [0.07075278490781815, 0.03203, 0, 1, 0.001, 0.00075, 4.958959793330959, 0], "E8.36.0.0": [0.075752784907818, 0.03203, 0, 1, 0.001, 0.0007199110732306023, 0, 1.3242255138486574], "E8.36.0.3": [0.07575278490781816, 0.03203, 0, 1, 0.001, 0.00075, 4.958959793330959, 0], "E8.37.0.0": [0.08075278490781801, 0.03203, 0, 1, 0.001, 0.0007199110732306023, 0, 1.3242255138486574], "E8.37.0.3": [0.08075278490781816, 0.03203, 0, 1, 0.001, 0.00075, 4.958959793330959, 0], "E8.38.0.0": [0.08575278490781801, 0.03203, 0, 1, 0.001, 0.0007199110732306023, 0, 1.3242255138486574], "E8.38.0.3": [0.08575278490781817, 0.03203, 0, 1, 0.001, 0.00075, 4.958959793330959, 0], "E8.39.0.0": [0.09075278490781802, 0.03203, 0, 1, 0.001, 0.0007199110732306023, 0, 1.3242255138486574], "E8.39.0.3": [0.09075278490781817, 0.03203, 0, 1, 0.001, 0.00075, 4.958959793330959, 0], "E9.1.0.1": [-0.10924721509218197, 0.03203, 0, 1, 0.001, 0.00075, 4.958959793331002, 0], "E9.1.0.2": [-0.10924721509218216, 0.03203, 0, 1, 0.001, 0.0007199110732306023, 0, 1.3242255138486574], "E9.2.0.1": [-0.11424721509218197, 0.03203, 0, 1, 0.001, 0.00075, 4.958959793331002, 0], "E9.2.0.2": [-0.11424721509218216, 0.03203, 0, 1, 0.001, 0.0007199110732306023, 0, 1.3242255138486574], "E9.3.0.1": [-0.11924721509218197, 0.03203, 0, 1, 0.001, 0.00075, 4.958959793331002, 0], "E9.3.0.2": [-0.11924721509218217, 0.03203, 0, 1, 0.001, 0.0007199110732306023, 0, 1.3242255138486574], "E9.4.0.1": [-0.12424721509218196, 0.03203, 0, 1, 0.001, 0.00075, 4.958959793331005, 0], "E9.4.0.2": [-0.12424721509218217, 0.03203, 0, 1, 0.001, 0.0007199110732306023, 0, 1.3242255138486574], "E9.5.0.1": [-0.12924721509218196, 0.03203, 0, 1, 0.001, 0.00075, 4.958959793331006, 0], "E9.5.0.2": [-0.12924721509218218, 0.03203, 0, 1, 0.001, 0.0007199110732306023, 0, 1.3242255138486574], "E9.6.0.1": [-0.13424721509218196, 0.03203, 0, 1, 0.001, 0.00075, 4.958959793331013, 0], "E9.6.0.2": [-0.13424721509218218, 0.03203, 0, 1, 0.001, 0.0007199110732306023, 0, 1.3242255138486574], "E9.7.0.1": [-0.13924721509218196, 0.03203, 0, 1, 0.001, 0.00075, 4.958959793331013, 0], "E9.7.0.2": [-0.13924721509218219, 0.03203, 0, 1, 0.001, 0.0007199110732306023, 0, 1.3242255138486574], "E9.8.0.1": [-0.14424721509218197, 0.03203, 0, 1, 0.001, 0.00075, 4.958959793331013, 0], "E9.8.0.2": [-0.1442472150921822, 0.03203, 0, 1, 0.001, 0.0007199110732306023, 0, 1.3242255138486574], "E10.8.0.0": [0.0521547044980927, -0.03203, 0, -1, 0.001, 0.00075, 4.958959793330937, 0], "E11.0.7.0": [0.0521547044980927, -0.03203, 0, -1, 0.001, 0.0007199110732306023, 0, 1.3242255138486587], "E12.1.0.0": [0.0471547044980927, -0.03203, 0, -1, 0.001, 0.0007199110732306023, 0, 1.324225513848658], "E12.1.0.3": [0.0471547044980927, -0.03203, 0, -1, 0.001, 0.00075, 4.95895979333093, 0], "E12.2.0.0": [0.04215470449809269, -0.03203, 0, -1, 0.001, 0.0007199110732306023, 0, 1.324225513848658], "E12.2.0.3": [0.04215470449809269, -0.03203, 0, -1, 0.001, 0.00075, 4.95895979333093, 0], "E12.3.0.0": [0.03715470449809269, -0.03203, 0, -1, 0.001, 0.0007199110732306023, 0, 1.324225513848658], "E12.3.0.3": [0.03715470449809269, -0.03203, 0, -1, 0.001, 0.00075, 4.958959793330925, 0], "E12.4.0.0": [0.032154704498092684, -0.03203, 0, -1, 0.001, 0.0007199110732306023, 0, 1.324225513848658], "E12.4.0.3": [0.032154704498092684, -0.03203, 0, -1, 0.001, 0.00075, 4.958959793330925, 0], "E12.5.0.0": [0.027154704498092683, -0.03203, 0, -1, 0.001, 0.0007199110732306023, 0, 1.324225513848658], "E12.5.0.3": [0.02715470449809268, -0.03203, 0, -1, 0.001, 0.00075, 4.958959793330931, 0], "E12.6.0.0": [0.02215470449809268, -0.03203, 0, -1, 0.001, 0.0007199110732306023, 0, 1.324225513848658], "E12.6.0.3": [0.022154704498092676, -0.03203, 0, -1, 0.001, 0.00075, 4.958959793330932, 0], "E12.7.0.0": [0.017154704498092675, -0.03203, 0, -1, 0.001, 0.0007199110732306023, 0, 1.324225513848658], "E12.7.0.3": [0.01715470449809267, -0.03203, 0, -1, 0.001, 0.00075, 4.958959793330933, 0], "E12.8.0.0": [0.01215470449809267, -0.03203, 0, -1, 0.001, 0.0007199110732306023, 0, 1.324225513848658], "E12.8.0.3": [0.012154704498092667, -0.03203, 0, -1, 0.001, 0.00075, 4.958959793330933, 0], "E12.9.0.0": [0.007154704498092666, -0.03203, 0, -1, 0.001, 0.0007199110732306023, 0, 1.324225513848658], "E12.9.0.3": [0.007154704498092662, -0.03203, 0, -1, 0.001, 0.00075, 4.958959793330933, 0], "E12.10.0.0": [0.002154704498092661, -0.03203, 0, -1, 0.001, 0.0007199110732306023, 0, 1.324225513848658], "E12.10.0.3": [0.0021547044980926577, -0.03203, 0, -1, 0.001, 0.00075, 4.958959793330933, 0], "E12.11.0.0": [-0.0028452955019073432, -0.03203, 0, -1, 0.001, 0.0007199110732306023, 0, 1.324225513848658], "E12.11.0.3": [-0.0028452955019073467, -0.03203, 0, -1, 0.001, 0.00075, 4.9589597933309335, 0], "E12.12.0.0": [-0.007845295501907348, -0.03203, 0, -1, 0.001, 0.0007199110732306023, 0, 1.324225513848658], "E12.12.0.3": [-0.007845295501907351, -0.03203, 0, -1, 0.001, 0.00075, 4.958959793330926, 0], "E12.13.0.0": [-0.012845295501907349, -0.03203, 0, -1, 0.001, 0.0007199110732306023, 0, 1.3242255138486587], "E12.13.0.3": [-0.012845295501907356, -0.03203, 0, -1, 0.001, 0.00075, 4.958959793330928, 0], "E12.14.0.0": [-0.017845295501907353, -0.03203, 0, -1, 0.001, 0.0007199110732306023, 0, 1.3242255138486587], "E12.14.0.3": [-0.01784529550190736, -0.03203, 0, -1, 0.001, 0.00075, 4.958959793330928, 0], "E12.15.0.0": [-0.022845295501907358, -0.03203, 0, -1, 0.001, 0.0007199110732306023, 0, 1.3242255138486587], "E12.15.0.3": [-0.022845295501907364, -0.03203, 0, -1, 0.001, 0.00075, 4.958959793330928, 0], "E12.16.0.0": [-0.027845295501907362, -0.03203, 0, -1, 0.001, 0.0007199110732306023, 0, 1.3242255138486587], "E12.16.0.3": [-0.02784529550190737, -0.03203, 0, -1, 0.001, 0.00075, 4.958959793330928, 0], "E12.17.0.0": [-0.032845295501907366, -0.03203, 0, -1, 0.001, 0.0007199110732306023, 0, 1.3242255138486587], "E12.17.0.3": [-0.03284529550190737, -0.03203, 0, -1, 0.001, 0.00075, 4.958959793330935, 0], "E12.18.0.0": [-0.03784529550190737, -0.03203, 0, -1, 0.001, 0.0007199110732306023, 0, 1.3242255138486587], "E12.18.0.3": [-0.03784529550190738, -0.03203, 0, -1, 0.001, 0.00075, 4.958959793330935, 0], "E12.19.0.0": [-0.04284529550190738, -0.03203, 0, -1, 0.001, 0.0007199110732306023, 0, 1.3242255138486574], "E12.19.0.3": [-0.04284529550190738, -0.03203, 0, -1, 0.001, 0.00075, 4.958959793330935, 0], "E12.20.0.0": [-0.04784529550190739, -0.03203, 0, -1, 0.001, 0.0007199110732306023, 0, 1.3242255138486574], "E12.20.0.3": [-0.04784529550190739, -0.03203, 0, -1, 0.001, 0.00075, 4.958959793330935, 0], "E12.21.0.0": [-0.05284529550190739, -0.03203, 0, -1, 0.001, 0.0007199110732306023, 0, 1.3242255138486574], "E12.21.0.3": [-0.05284529550190739, -0.03203, 0, -1, 0.001, 0.00075, 4.958959793330932, 0], "E12.22.0.0": [-0.057845295501907396, -0.03203, 0, -1, 0.001, 0.0007199110732306023, 0, 1.3242255138486574], "E12.22.0.3": [-0.057845295501907396, -0.03203, 0, -1, 0.001, 0.00075, 4.958959793330932, 0], "E12.23.0.0": [-0.0628452955019074, -0.03203, 0, -1, 0.001, 0.0007199110732306023, 0, 1.3242255138486574], "E12.23.0.3": [-0.0628452955019074, -0.03203, 0, -1, 0.001, 0.00075, 4.958959793330932, 0], "E12.24.0.0": [-0.0678452955019074, -0.03203, 0, -1, 0.001, 0.0007199110732306023, 0, 1.3242255138486574], "E12.24.0.3": [-0.0678452955019074, -0.03203, 0, -1, 0.001, 0.00075, 4.958959793330932, 0], "E12.25.0.0": [-0.07284529550190741, -0.03203, 0, -1, 0.001, 0.0007199110732306023, 0, 1.3242255138486574], "E12.25.0.3": [-0.07284529550190741, -0.03203, 0, -1, 0.001, 0.00075, 4.958959793330927, 0], "E12.26.0.0": [-0.07784529550190741, -0.03203, 0, -1, 0.001, 0.0007199110732306023, 0, 1.3242255138486574], "E12.26.0.3": [-0.07784529550190741, -0.03203, 0, -1, 0.001, 0.00075, 4.958959793330927, 0], "E12.27.0.0": [-0.08284529550190742, -0.03203, 0, -1, 0.001, 0.0007199110732306023, 0, 1.3242255138486574], "E12.27.0.3": [-0.08284529550190742, -0.03203, 0, -1, 0.001, 0.00075, 4.958959793330927, 0], "E12.28.0.0": [-0.08784529550190742, -0.03203, 0, -1, 0.001, 0.0007199110732306023, 0, 1.3242255138486574], "E12.28.0.3": [-0.08784529550190742, -0.03203, 0, -1, 0.001, 0.00075, 4.958959793330927, 0], "E12.29.0.0": [-0.09284529550190743, -0.03203, 0, -1, 0.001, 0.0007199110732306023, 0, 1.3242255138486574], "E12.29.0.3": [-0.09284529550190743, -0.03203, 0, -1, 0.001, 0.00075, 4.9589597933309335, 0], "E12.30.0.0": [-0.09784529550190743, -0.03203, 0, -1, 0.001, 0.0007199110732306023, 0, 1.3242255138486574], "E12.30.0.3": [-0.09784529550190743, -0.03203, 0, -1, 0.001, 0.00075, 4.9589597933309335, 0], "E12.31.0.0": [-0.10284529550190744, -0.03203, 0, -1, 0.001, 0.0007199110732306023, 0, 1.3242255138486574], "E12.31.0.3": [-0.10284529550190744, -0.03203, 0, -1, 0.001, 0.00075, 4.9589597933309335, 0], "E12.32.0.0": [-0.10784529550190744, -0.03203, 0, -1, 0.001, 0.0007199110732306023, 0, 1.3242255138486574], "E12.32.0.3": [-0.10784529550190744, -0.03203, 0, -1, 0.001, 0.00075, 4.9589597933309335, 0], "E12.33.0.0": [-0.11284529550190744, -0.03203, 0, -1, 0.001, 0.0007199110732306023, 0, 1.3242255138486574], "E12.33.0.3": [-0.11284529550190744, -0.03203, 0, -1, 0.001, 0.00075, 4.9589597933309335, 0], "E12.34.0.0": [-0.11784529550190745, -0.03203, 0, -1, 0.001, 0.0007199110732306023, 0, 1.3242255138486574], "E12.34.0.3": [-0.11784529550190745, -0.03203, 0, -1, 0.001, 0.00075, 4.9589597933309335, 0], "E12.35.0.0": [-0.12284529550190745, -0.03203, 0, -1, 0.001, 0.0007199110732306023, 0, 1.3242255138486574], "E12.35.0.3": [-0.12284529550190745, -0.03203, 0, -1, 0.001, 0.00075, 4.958959793330927, 0], "E12.36.0.0": [-0.12784529550190746, -0.03203, 0, -1, 0.001, 0.0007199110732306023, 0, 1.3242255138486574], "E12.36.0.3": [-0.12784529550190746, -0.03203, 0, -1, 0.001, 0.00075, 4.958959793330927, 0], "E12.37.0.0": [-0.13284529550190746, -0.03203, 0, -1, 0.001, 0.0007199110732306023, 0, 1.3242255138486574], "E12.37.0.3": [-0.13284529550190746, -0.03203, 0, -1, 0.001, 0.00075, 4.958959793330927, 0], "E12.38.0.0": [-0.13784529550190747, -0.03203, 0, -1, 0.001, 0.0007199110732306023, 0, 1.3242255138486574], "E12.38.0.3": [-0.13784529550190747, -0.03203, 0, -1, 0.001, 0.00075, 4.958959793330927, 0], "E12.39.0.0": [-0.14284529550190747, -0.03203, 0, -1, 0.001, 0.0007199110732306023, 0, 1.3242255138486574], "E12.39.0.3": [-0.14284529550190747, -0.03203, 0, -1, 0.001, 0.00075, 4.958959793330927, 0], "E13.1.0.1": [0.05715470449809271, -0.03203, 0, -1, 0.001, 0.00075, 4.958959793330936, 0], "E13.1.0.2": [0.057154704498092714, -0.03203, 0, -1, 0.001, 0.0007199110732306023, 0, 1.3242255138486587], "E13.2.0.1": [0.06215470449809271, -0.03203, 0, -1, 0.001, 0.00075, 4.958959793330934, 0], "E13.2.0.2": [0.06215470449809272, -0.03203, 0, -1, 0.001, 0.0007199110732306023, 0, 1.3242255138486587], "E13.3.0.1": [0.06715470449809272, -0.03203, 0, -1, 0.001, 0.00075, 4.958959793330934, 0], "E13.3.0.2": [0.06715470449809272, -0.03203, 0, -1, 0.001, 0.0007199110732306023, 0, 1.3242255138486587], "E13.4.0.1": [0.07215470449809272, -0.03203, 0, -1, 0.001, 0.00075, 4.958959793330932, 0], "E13.4.0.2": [0.07215470449809272, -0.03203, 0, -1, 0.001, 0.0007199110732306023, 0, 1.3242255138486587], "E13.5.0.1": [0.07715470449809272, -0.03203, 0, -1, 0.001, 0.00075, 4.958959793330932, 0], "E13.5.0.2": [0.07715470449809272, -0.03203, 0, -1, 0.001, 0.0007199110732306023, 0, 1.3242255138486587], "E13.6.0.1": [0.08215470449809273, -0.03203, 0, -1, 0.001, 0.00075, 4.9589597933309255, 0], "E13.6.0.2": [0.08215470449809273, -0.03203, 0, -1, 0.001, 0.0007199110732306023, 0, 1.3242255138486587], "E13.7.0.1": [0.08715470449809273, -0.03203, 0, -1, 0.001, 0.00075, 4.9589597933309255, 0], "E13.7.0.2": [0.08715470449809273, -0.03203, 0, -1, 0.001, 0.0007199110732306023, 0, 1.3242255138486574], "E13.8.0.1": [0.09215470449809274, -0.03203, 0, -1, 0.001, 0.00075, 4.95895979333093, 0], "E13.8.0.2": [0.09215470449809274, -0.03203, 0, -1, 0.001, 0.0007199110732306023, 0, 1.3242255138486574], "E14.1.1": [-0.1471758775437171, -0.03225100571911596, -0.13413031666450417, -0.9909637017325508, 0.001, 0.00075, 4.958959793330923, 6.283185307179578], "E14.1.2": [-0.14717587754371714, -0.03225100571911596, -0.1341303166645044, -0.9909637017325508, 0.001, 0.0007199110732306023, 0, 1.3242255138486576], "E14.2.1": [-0.15149697072161497, -0.03188915202402568, -0.2658365502328327, -0.9640181163029597, 0.001, 0.00075, 4.958959793330916, 0], "E14.2.2": [-0.15149697072161497, -0.03188915202402569, -0.2658365502328329, -0.9640181163029596, 0.001, 0.0007199110732306023, 0, 1.3242255138486558], "E14.3.1": [-0.1557304816620073, -0.030950978550565136, -0.39273842708457396, -0.9196502204050924, 0.001, 0.00075, 4.958959793330917, 0], "E14.3.2": [-0.15573048166200723, -0.030950978550565146, -0.3927384270845742, -0.9196502204050923, 0.001, 0.0007199110732306023, 0, 1.3242255138486487], "E14.4.1": [-0.15979989982974216, -0.029453440529399938, -0.5125425007998651, -0.8586618571206133, 0.001, 0.00075, 4.958959793330927, 6.283185307179571], "E14.4.2": [-0.15979989982974213, -0.029453440529399952, -0.5125425007998653, -0.8586618571206132, 0.001, 0.0007199110732306023, 6.283185307179571, 1.3242255138486505], "E14.5.1": [-0.16363168027214237, -0.02742360236098225, -0.6230836006912123, -0.7821552445324866, 0.001, 0.00075, 4.958959793330966, 6.283185307179584], "E14.5.2": [-0.1636316802721424, -0.02742360236098229, -0.6230836006912126, -0.7821552445324864, 0.001, 0.0007199110732306023, 6.2831853071795845, 1.3242255138486532], "E14.6.1": [-0.16715657276726215, -0.02489814849156105, -0.7223639620597555, -0.6915130557822696, 0.001, 0.00075, 4.95895979333095, 6.283185307179573], "E14.6.2": [-0.16715657276726215, -0.024898148491561092, -0.7223639620597556, -0.6915130557822693, 0.001, 0.0007199110732306023, 6.283185307179573, 1.324225513848668], "E14.7.1": [-0.17031087335520825, -0.021922720429985887, -0.808589330990642, -0.5883734305762848, 0.001, 0.00075, 4.958959793330919, 6.283185307179582], "E14.7.2": [-0.17031087335520823, -0.021922720429985915, -0.8085893309906422, -0.5883734305762844, 0.001, 0.0007199110732306023, 6.283185307179582, 1.324225513848661], "E14.8.1": [-0.17303757563410496, -0.018551091887132165, -0.8802013911801112, -0.4746003697476406, 0.001, 0.00075, 4.958959793330942, 6.283185307179585], "E14.8.2": [-0.17303757563410493, -0.018551091887132207, -0.8802013911801112, -0.4746003697476403, 0.001, 0.0007199110732306023, 6.283185307179585, 1.3242255138486378], "E14.9.1": [-0.17528740101379497, -0.01484419694532052, -0.9359059267573256, -0.3522500479212337, 0.001, 0.00075, 4.95895979333092, 0], "E14.9.2": [-0.17528740101379497, -0.014844196945320562, -0.9359059267573258, -0.3522500479212335, 0.001, 0.0007199110732306023, 0, 1.3242255138486556], "E14.10.1": [-0.17701968930791717, -0.010869028821231502, -0.9746962121256348, -0.22353365309934756, 0.001, 0.00075, 4.95895979333096, 6.283185307179582], "E14.10.2": [-0.17701968930791717, -0.010869028821231558, -0.9746962121256348, -0.22353365309934733, 0.001, 0.0007199110732306023, 6.283185307179582, 1.3242255138486432], "E14.11.1": [-0.1782031335690498, -0.006697429124530224, -0.9958712061081035, -0.09077742475302515, 0.001, 0.00075, 4.958959793330939, 6.283185307179585], "E14.11.2": [-0.1782031335690498, -0.006697429124530252, -0.9958712061081036, -0.09077742475302492, 0.001, 0.0007199110732306023, 6.2831853071795845, 1.3242255138486558], "E14.12.1": [-0.1788163458865398, -0.002404789493440196, -0.9990482215818578, 0.04361938736533578, 0.001, 0.00075, 4.958959793330969, 0], "E14.12.2": [-0.17881634588653983, -0.0024047894934402514, -0.9990482215818578, 0.043619387365336014, 0.001, 0.0007199110732306023, 0, 1.324225513848648], "E14.13.1": [-0.178848243921583, 0.0019313109279160967, -0.9841698416280553, 0.17722788389474375, 0.001, 0.00075, 4.958959793330945, 6.283185307179585], "E14.13.2": [-0.17884824392158302, 0.0019313109279160967, -0.9841698416280552, 0.17722788389474395, 0.001, 0.0007199110732306023, 6.283185307179585, 1.3242255138486554], "E14.14.1": [-0.17829825119386178, 0.006232507546088756, -0.9515049572046939, 0.307633412383788, 0.001, 0.00075, 4.95895979333097, 0], "E14.14.2": [-0.1782982511938618, 0.006232507546088756, -0.9515049572046937, 0.3076334123837882, 0.001, 0.0007199110732306023, 0, 1.3242255138486425], "E14.15.1": [-0.17717630750004143, 0.010421066569980264, -0.9016439075888162, 0.43247920633016623, 0.001, 0.00075, 4.958959793330932, 0], "E14.15.2": [-0.17717630750004143, 0.010421066569980264, -0.9016439075888161, 0.43247920633016645, 0.001, 0.0007199110732306023, 6.283185307179585, 1.324225513848673], "E14.16.1": [-0.17550268927583512, 0.01442128986228916, -0.8354878114129366, 0.5495089780708059, 0.001, 0.00075, 4.958959793330958, 6.283185307179584], "E14.16.2": [-0.17550268927583512, 0.014421289862289174, -0.8354878114129364, 0.5495089780708062, 0.001, 0.0007199110732306023, 6.283185307179583, 1.3242255138486299], "E14.17.1": [-0.17330764314816255, 0.0181608830014041, -0.7542322811115656, 0.6566076957584677, 0.001, 0.00075, 4.958959793330877, 0], "E14.17.2": [-0.17330764314816255, 0.0181608830014041, -0.7542322811115654, 0.6566076957584679, 0.001, 0.0007199110732306023, 0, 1.324225513848695], "E14.18.1": [-0.1706308393000644, 0.021572261829317166, -0.6593458151000691, 0.7518398074789773, 0.001, 0.00075, 4.9589597933309895, 0], "E14.18.2": [-0.17063083930006445, 0.021572261829317166, -0.6593458151000688, 0.7518398074789774, 0.001, 0.0007199110732306023, 0, 1.3242255138486523], "E14.19.1": [-0.16752065452749068, 0.02459377387284381, -0.552543258195295, 0.8334842217000438, 0.001, 0.00075, 4.958959793330924, 6.283185307179578], "E14.19.2": [-0.16752065452749068, 0.024593773872843797, -0.5525432581952947, 0.833484221700044, 0.001, 0.0007199110732306023, 6.283185307179576, 1.3242255138486605], "E14.20.1": [-0.16403329794498497, 0.027170812563896016, -0.4357548099170794, 0.9000654118641211, 0.001, 0.00075, 4.9589597933309, 0], "E14.20.2": [-0.164033297944985, 0.027170812563896002, -0.4357548099170792, 0.9000654118641213, 0.001, 0.0007199110732306023, 0, 1.324225513848679], "E14.21.1": [-0.1602317951410362, 0.029256804121955547, -0.311091140771091, 0.9503800829845612, 0.001, 0.00075, 4.958959793330925, 0], "E14.21.2": [-0.16023179514103622, 0.029256804121955547, -0.3110911407710908, 0.9503800829845612, 0.001, 0.0007199110732306023, 0, 1.324225513848667], "E14.22.1": [-0.15618484914204636, 0.03081404926321844, -0.18080524695236547, 0.9835189183104177, 0.001, 0.00075, 4.958959793330942, 6.28318530717957], "E14.22.2": [-0.15618484914204644, 0.03081404926321844, -0.18080524695236525, 0.9835189183104178, 0.001, 0.0007199110732306023, 6.283185307179569, 1.3242255138486603], "E14.23.1": [-0.15196559877025392, 0.03181440452454069, -0.047251732854076835, 0.9988830130412104, 0.001, 0.00075, 4.958959793330928, 0], "E14.23.2": [-0.15196559877025398, 0.0318144045245407, -0.047251732854076835, 0.9988830130412105, 0.001, 0.0007199110732306023, 0, 1.3242255138486554], "E14.24.1": [-0.14765029683530784, 0.03223979088889288, 0.08715574274765807, 0.9961946980917455, 0.001, 0.00075, 4.958959793330928, 0], "E14.24.2": [-0.14765029683530784, 0.03223979088889289, 0.08715574274765807, 0.9961946980917457, 0.001, 0.0007199110732306023, 0, 1.3242255138486732], "E15.1.1": [0.09546476511906711, 0.03206534447433594, 0.1462399908993832, 0.9892491420576256, 0.001, 0.00075, 4.958959793330953, 0], "E15.1.2": [0.09546476511906697, 0.032065344474335955, 0.14623999089937964, 0.9892491420576262, 0.001, 0.0007199110732306023, 0, 1.3242255138486574], "E15.2.1": [0.10013125627604288, 0.031411229022038134, 0.289335571063456, 0.9572277301234978, 0.001, 0.00075, 4.958959793330956, 6.283185307179577], "E15.2.2": [0.10013125627604275, 0.031411229022038176, 0.28933557106345276, 0.9572277301234989, 0.001, 0.0007199110732306023, 0, 1.3242255138486574], "E15.3.1": [0.10465192081170949, 0.03008171824771774, 0.42620993998317114, 0.9046242794992525, 0.001, 0.00075, 4.958959793330948, 0], "E15.3.2": [0.10465192081170938, 0.030081718247717788, 0.42620993998316825, 0.9046242794992538, 0.001, 0.0007199110732306023, 0, 1.3242255138486574], "E15.4.1": [0.10892955668161075, 0.02810539891430988, 0.5539200638661127, 0.8325698546347697, 0.001, 0.00075, 4.958959793330958, 0], "E15.4.2": [0.10892955668161065, 0.02810539891430995, 0.5539200638661103, 0.8325698546347714, 0.001, 0.0007199110732306023, 0, 1.3242255138486574], "E15.5.1": [0.11287218737461369, 0.025524765278619035, 0.669719955912944, 0.7426137493017244, 0.001, 0.00075, 4.95895979333094, 6.283185307179585], "E15.5.2": [0.11287218737461359, 0.025524765278619105, 0.6697199559129419, 0.7426137493017263, 0.001, 0.0007199110732306023, 0, 1.3242255138486574], "E15.6.1": [0.11639503956571884, 0.022395305391882447, 0.7711197197453893, 0.6366901741190863, 0.001, 0.00075, 4.958959793330943, 0], "E15.6.2": [0.11639503956571878, 0.022395305391882517, 0.7711197197453877, 0.6366901741190883, 0.001, 0.0007199110732306023, 0, 1.3242255138486574], "E15.7.1": [0.11942236588800911, 0.01878430801145746, 0.8559390864507429, 0.517076667705929, 0.001, 0.00075, 4.958959793330941, 6.283185307179584], "E15.7.2": [0.11942236588800906, 0.018784308011457536, 0.8559390864507416, 0.5170766677059311, 0.001, 0.0007199110732306023, 0, 1.3242255138486574], "E15.8.1": [0.12188907363101217, 0.01476941577707859, 0.9223542941045814, 0.3863451256931288, 0.001, 0.00075, 4.958959793330928, 0], "E15.8.2": [0.12188907363101217, 0.01476941577707859, 0.9223542941045814, 0.3863451256931288, 0.001, 0.0007199110732306023, 0, 1.3242255138486574], "E15.9.1": [0.12374212434566731, 0.010436955760877178, 0.9689373017815074, 0.2473065005542154, 0.001, 0.00075, 4.958959793330928, 0], "E15.9.2": [0.12374212434566731, 0.010436955760877178, 0.9689373017815074, 0.2473065005542154, 0.001, 0.0007199110732306023, 0, 1.3242255138486574], "E15.10.1": [0.12494167426198798, 0.005880083287203713, 0.9946864948853934, 0.10295036130393434, 0.001, 0.00075, 4.958959793330928, 0], "E15.10.2": [0.12494167426198798, 0.005880083287203811, 0.9946864948853931, 0.10295036130393653, 0.001, 0.0007199110732306023, 0, 1.3242255138486556], "E15.11.1": [0.12546193099848385, 0.001196778933310147, 0.9990482215818578, -0.04361938736533589, 0.001, 0.00075, 4.958959793330928, 0], "E15.11.2": [0.12546193099848385, 0.001196778933310258, 0.9990482215818579, -0.04361938736533366, 0.001, 0.0007199110732306023, 0, 1.3242255138486327], "E15.12.1": [0.12529170814261967, -0.003512258221184311, 0.9819286972627069, -0.18925124436041016, 0.001, 0.00075, 4.958959793330928, 0], "E15.12.2": [0.1252917081426197, -0.0035122582211842, 0.9819286972627073, -0.18925124436040774, 0.001, 0.0007199110732306023, 0, 1.3242255138486299], "E15.13.1": [0.12443466577787932, -0.008145775797292976, 0.9436960210759326, -0.33081387486841185, 0.001, 0.00075, 4.958959793330928, 0], "E15.13.2": [0.12443466577787936, -0.008145775797292892, 0.9436960210759334, -0.33081387486840935, 0.001, 0.0007199110732306023, 6.283185307179583, 1.324225513848656], "E15.14.1": [0.12290923178569063, -0.012604145216547416, 0.8851722611624167, -0.46526343942826026, 0.001, 0.00075, 4.958959793330928, 0], "E15.14.2": [0.1229092317856907, -0.012604145216547319, 0.8851722611624179, -0.4652634394282579, 0.001, 0.0007199110732306023, 6.283185307179584, 1.3242255138486483], "E15.15.1": [0.12074820561435459, -0.016791503886385548, 0.8076157787803266, -0.589709041701962, 0.001, 0.00075, 4.958959793330928, 0], "E15.15.2": [0.12074820561435469, -0.01679150388638545, 0.8076157787803285, -0.5897090417019595, 0.001, 0.0007199110732306023, 0, 1.3242255138486472], "E15.16.1": [0.1179980530346268, -0.020617816410380976, 0.712694171378863, -0.701474887706321, 0.001, 0.00075, 4.958959793330928, 0], "E15.16.2": [0.11799805303462689, -0.02061781641038088, 0.7126941713788653, -0.7014748877063188, 0.001, 0.0007199110732306023, 0, 1.3242255138486345], "E15.17.1": [0.11471790704591622, -0.02400081050375652, 0.6024484163916951, -0.7981578199749337, 0.001, 0.00075, 4.958959793330928, 0], "E15.17.2": [0.11471790704591633, -0.02400081050375643, 0.602448416391698, -0.7981578199749316, 0.001, 0.0007199110732306023, 0, 1.3242255138486227], "E15.18.1": [0.11097829641533262, -0.026867745988676597, 0.4792489867200568, -0.8776789895672559, 0.001, 0.00075, 4.958959793330928, 0], "E15.18.2": [0.11097829641533276, -0.026867745988676535, 0.4792489867200602, -0.8776789895672539, 0.001, 0.0007199110732306023, 6.283185307179579, 1.324225513848639], "E15.19.1": [0.1068596291881744, -0.029156978832884595, 0.3457448814979111, -0.9383285548878897, 0.001, 0.00075, 4.958959793330928, 0], "E15.19.2": [0.10685962918817452, -0.029156978832884532, 0.3457448814979145, -0.9383285548878885, 0.001, 0.0007199110732306023, 6.283185307179583, 1.324225513848611], "E15.20.1": [0.10245046377698372, -0.0308192866021703, 0.2048066680651905, -0.9788024462147787, 0.001, 0.00075, 4.958959793330928, 0], "E15.20.2": [0.10245046377698389, -0.03081928660217025, 0.20480666806519485, -0.9788024462147779, 0.001, 0.0007199110732306023, 6.283185307179577, 1.3242255138486068], "E15.21.1": [0.09784560480372088, -0.031818926827165514, 0.059464759844431565, -0.9982304054358613, 0.001, 0.00075, 4.958959793330928, 0], "E15.21.2": [0.09784560480372106, -0.03181892682716549, 0.059464759844435555, -0.9982304054358611, 0.001, 0.0007199110732306023, 6.283185307179582, 1.3242255138486099]};
            skSetInitialGuess(sketch, initialGuessF0);
            skSolve(sketch);
        }
        {
            var Q0;
            Q0=makeQuery(id+"F0.imprint","IMPRINT",FACE,{"disambiguationData":[TD([[makeQuery(id+"F0.imprint","IMPRINT",EDGE,{"derivedFrom":sQuery(id+"F0.wireOp",EDGE,"E0")}),1.0]])]});
            extrude(context, id + "F1", {"entities" : qUnion([Q0]), "depth" : 10 * mm, "offsetDistance" : 25 * mm});
        }
    });
